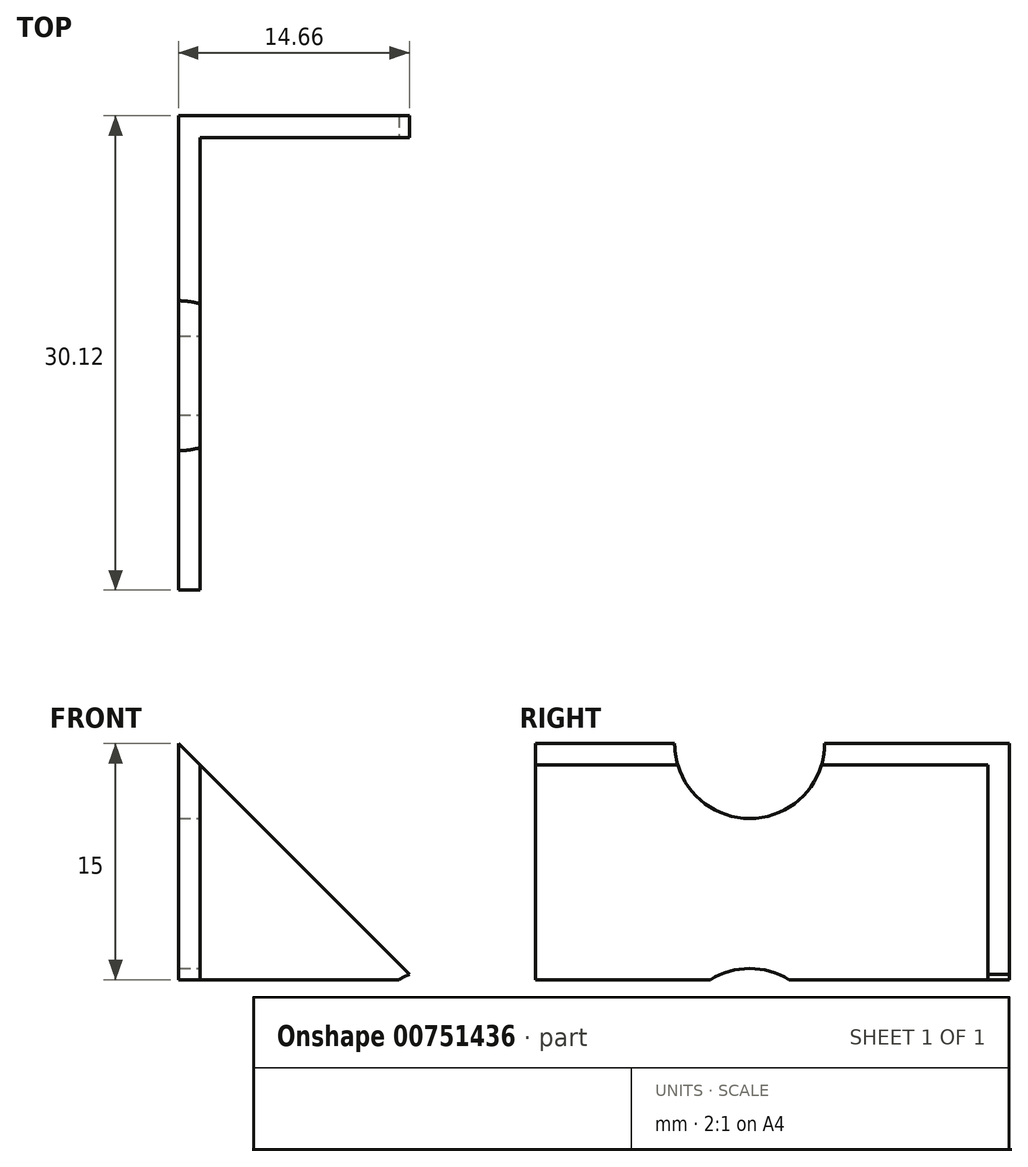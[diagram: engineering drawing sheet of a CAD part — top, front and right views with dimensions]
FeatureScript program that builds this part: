
annotation { "Feature Type Name" : "Feature", "Feature Type Description" : "" }
export const myFeature = defineFeature(function(context is Context, id is Id, definition is map)
    precondition{}
    {
        {
            assignVariable(context, id + "F0", {"name" : "height", "anyValue" : 15});
        }
        {
            var Q0;
            Q0=qCreatedBy(makeId("Top.planeOp"),FACE);
            var sketch = newSketch(context, id + "F1", { "sketchPlane" : qUnion([Q0])});
            skLineSegment(sketch, "E0", {"start": v(-1.37, -28.75) * mm, "end": v(-1.37, 1.37) * mm});
            skLineSegment(sketch, "E1", {"start": v(-1.37, 1.37) * mm, "end": v(28.75, 1.37) * mm});
            skLineSegment(sketch, "E2", {"start": v(28.75, 1.37) * mm, "end": v(28.75, 0) * mm});
            skLineSegment(sketch, "E3", {"start": v(28.75, 0) * mm, "end": v(0, 0) * mm});
            skLineSegment(sketch, "E4", {"start": v(0, 0) * mm, "end": v(0, -28.75) * mm});
            skLineSegment(sketch, "E5", {"start": v(0, -28.75) * mm, "end": v(-1.37, -28.75) * mm});
            skSolve(sketch);
        }
        {
            var Q0;
            Q0=makeQuery(id+"F1.imprint","IMPRINT",FACE,{"disambiguationData":[TD([[makeQuery(id+"F1.imprint","IMPRINT",EDGE,{"derivedFrom":sQuery(id+"F1.wireOp",EDGE,"E0")}),-1.0]])]});
            extrude(context, id + "F2", {"entities" : qUnion([Q0]), "depth" : (getVariable(context, 'height')) * mm, "offsetDistance" : 25.4 * mm});
        }
        {
            var Q0;
            Q0=makeQuery(id+"F2.opExtrude","SWEPT_FACE",FACE,{"disambiguationData":[OSD([sQuery(id+"F1.wireOp",EDGE,"E3")])]});
            var sketch = newSketch(context, id + "F3", { "sketchPlane" : qUnion([Q0])});
            skPoint(sketch, "E6", {"position": v(15.14, 19.05) * mm});
            skLineSegment(sketch, "E7", {"start": v(15.14, 0) * mm, "end": v(15.14, 381) * mm, "construction": true});
            skCircle(sketch, "E8", {"center": v(15.14, 19.05) * mm, "radius": 4.76 * mm});
            skCircle(sketch, "E9", {"center": v(15.14, 0) * mm, "radius": 4.76 * mm});
            skPoint(sketch, "E10", {"position": v(15.14, 38.1) * mm});
            skPoint(sketch, "E11", {"position": v(15.14, 57.15) * mm});
            skArc(sketch, "E12", {"start": v(19.9, 39.69) * mm, "mid": v(15.14, 44.45) * mm, "end": v(10.38, 39.69) * mm});
            skArc(sketch, "E13", {"start": v(10.38, 36.51) * mm, "mid": v(15.14, 31.75) * mm, "end": v(19.9, 36.51) * mm});
            skLineSegment(sketch, "E14", {"start": v(19.9, 39.69) * mm, "end": v(19.9, 36.51) * mm});
            skLineSegment(sketch, "E15", {"start": v(10.38, 39.69) * mm, "end": v(10.38, 36.51) * mm});
            skArc(sketch, "E16", {"start": v(19.9, 58.74) * mm, "mid": v(15.14, 63.5) * mm, "end": v(10.38, 58.74) * mm});
            skArc(sketch, "E17", {"start": v(10.38, 55.56) * mm, "mid": v(15.14, 50.8) * mm, "end": v(19.9, 55.56) * mm});
            skLineSegment(sketch, "E18", {"start": v(19.9, 58.74) * mm, "end": v(19.9, 55.56) * mm});
            skLineSegment(sketch, "E19", {"start": v(10.38, 58.74) * mm, "end": v(10.38, 55.56) * mm});
            skPoint(sketch, "E20.0.1.0", {"position": v(15.14, 133.35) * mm});
            skArc(sketch, "E20.0.1.1", {"start": v(19.9, 134.94) * mm, "mid": v(15.14, 139.7) * mm, "end": v(10.38, 134.94) * mm});
            skPoint(sketch, "E20.0.1.2", {"position": v(15.14, 114.3) * mm});
            skPoint(sketch, "E20.0.1.3", {"position": v(15.14, 95.25) * mm});
            skArc(sketch, "E20.0.1.4", {"start": v(10.38, 131.76) * mm, "mid": v(15.14, 127) * mm, "end": v(19.9, 131.76) * mm});
            skCircle(sketch, "E20.0.1.5", {"center": v(15.14, 95.25) * mm, "radius": 4.76 * mm});
            skCircle(sketch, "E20.0.1.6", {"center": v(15.14, 76.2) * mm, "radius": 4.76 * mm});
            skArc(sketch, "E20.0.1.7", {"start": v(19.9, 115.89) * mm, "mid": v(15.14, 120.65) * mm, "end": v(10.38, 115.89) * mm});
            skArc(sketch, "E20.0.1.8", {"start": v(10.38, 112.71) * mm, "mid": v(15.14, 107.95) * mm, "end": v(19.9, 112.71) * mm});
            skPoint(sketch, "E20.0.1.9", {"position": v(15.14, 133.35) * mm});
            skPoint(sketch, "E20.0.1.10", {"position": v(15.14, 114.3) * mm});
            skLineSegment(sketch, "E20.0.1.11", {"start": v(10.38, 134.94) * mm, "end": v(10.38, 131.76) * mm});
            skLineSegment(sketch, "E20.0.1.12", {"start": v(19.9, 134.94) * mm, "end": v(19.9, 131.76) * mm});
            skLineSegment(sketch, "E20.0.1.13", {"start": v(19.9, 115.89) * mm, "end": v(19.9, 112.71) * mm});
            skLineSegment(sketch, "E20.0.1.14", {"start": v(10.38, 115.89) * mm, "end": v(10.38, 112.71) * mm});
            skPoint(sketch, "E20.0.2.0", {"position": v(15.14, 209.55) * mm});
            skArc(sketch, "E20.0.2.1", {"start": v(19.9, 211.14) * mm, "mid": v(15.14, 215.9) * mm, "end": v(10.38, 211.14) * mm});
            skPoint(sketch, "E20.0.2.2", {"position": v(15.14, 190.5) * mm});
            skPoint(sketch, "E20.0.2.3", {"position": v(15.14, 171.45) * mm});
            skArc(sketch, "E20.0.2.4", {"start": v(10.38, 207.96) * mm, "mid": v(15.14, 203.2) * mm, "end": v(19.9, 207.96) * mm});
            skCircle(sketch, "E20.0.2.5", {"center": v(15.14, 171.45) * mm, "radius": 4.76 * mm});
            skCircle(sketch, "E20.0.2.6", {"center": v(15.14, 152.4) * mm, "radius": 4.76 * mm});
            skArc(sketch, "E20.0.2.7", {"start": v(19.9, 192.09) * mm, "mid": v(15.14, 196.85) * mm, "end": v(10.38, 192.09) * mm});
            skArc(sketch, "E20.0.2.8", {"start": v(10.38, 188.91) * mm, "mid": v(15.14, 184.15) * mm, "end": v(19.9, 188.91) * mm});
            skPoint(sketch, "E20.0.2.9", {"position": v(15.14, 209.55) * mm});
            skPoint(sketch, "E20.0.2.10", {"position": v(15.14, 190.5) * mm});
            skLineSegment(sketch, "E20.0.2.11", {"start": v(10.38, 211.14) * mm, "end": v(10.38, 207.96) * mm});
            skLineSegment(sketch, "E20.0.2.12", {"start": v(19.9, 211.14) * mm, "end": v(19.9, 207.96) * mm});
            skLineSegment(sketch, "E20.0.2.13", {"start": v(19.9, 192.09) * mm, "end": v(19.9, 188.91) * mm});
            skLineSegment(sketch, "E20.0.2.14", {"start": v(10.38, 192.09) * mm, "end": v(10.38, 188.91) * mm});
            skPoint(sketch, "E20.0.3.0", {"position": v(15.14, 285.75) * mm});
            skArc(sketch, "E20.0.3.1", {"start": v(19.9, 287.34) * mm, "mid": v(15.14, 292.1) * mm, "end": v(10.38, 287.34) * mm});
            skPoint(sketch, "E20.0.3.2", {"position": v(15.14, 266.7) * mm});
            skPoint(sketch, "E20.0.3.3", {"position": v(15.14, 247.65) * mm});
            skArc(sketch, "E20.0.3.4", {"start": v(10.38, 284.16) * mm, "mid": v(15.14, 279.4) * mm, "end": v(19.9, 284.16) * mm});
            skCircle(sketch, "E20.0.3.5", {"center": v(15.14, 247.65) * mm, "radius": 4.76 * mm});
            skCircle(sketch, "E20.0.3.6", {"center": v(15.14, 228.6) * mm, "radius": 4.76 * mm});
            skArc(sketch, "E20.0.3.7", {"start": v(19.9, 268.29) * mm, "mid": v(15.14, 273.05) * mm, "end": v(10.38, 268.29) * mm});
            skArc(sketch, "E20.0.3.8", {"start": v(10.38, 265.11) * mm, "mid": v(15.14, 260.35) * mm, "end": v(19.9, 265.11) * mm});
            skPoint(sketch, "E20.0.3.9", {"position": v(15.14, 285.75) * mm});
            skPoint(sketch, "E20.0.3.10", {"position": v(15.14, 266.7) * mm});
            skLineSegment(sketch, "E20.0.3.11", {"start": v(10.38, 287.34) * mm, "end": v(10.38, 284.16) * mm});
            skLineSegment(sketch, "E20.0.3.12", {"start": v(19.9, 287.34) * mm, "end": v(19.9, 284.16) * mm});
            skLineSegment(sketch, "E20.0.3.13", {"start": v(19.9, 268.29) * mm, "end": v(19.9, 265.11) * mm});
            skLineSegment(sketch, "E20.0.3.14", {"start": v(10.38, 268.29) * mm, "end": v(10.38, 265.11) * mm});
            skPoint(sketch, "E20.0.4.0", {"position": v(15.14, 361.95) * mm});
            skArc(sketch, "E20.0.4.1", {"start": v(19.9, 363.54) * mm, "mid": v(15.14, 368.3) * mm, "end": v(10.38, 363.54) * mm});
            skPoint(sketch, "E20.0.4.2", {"position": v(15.14, 342.9) * mm});
            skPoint(sketch, "E20.0.4.3", {"position": v(15.14, 323.85) * mm});
            skArc(sketch, "E20.0.4.4", {"start": v(10.38, 360.36) * mm, "mid": v(15.14, 355.6) * mm, "end": v(19.9, 360.36) * mm});
            skCircle(sketch, "E20.0.4.5", {"center": v(15.14, 323.85) * mm, "radius": 4.76 * mm});
            skCircle(sketch, "E20.0.4.6", {"center": v(15.14, 304.8) * mm, "radius": 4.76 * mm});
            skArc(sketch, "E20.0.4.7", {"start": v(19.9, 344.49) * mm, "mid": v(15.14, 349.25) * mm, "end": v(10.38, 344.49) * mm});
            skArc(sketch, "E20.0.4.8", {"start": v(10.38, 341.31) * mm, "mid": v(15.14, 336.55) * mm, "end": v(19.9, 341.31) * mm});
            skPoint(sketch, "E20.0.4.9", {"position": v(15.14, 361.95) * mm});
            skPoint(sketch, "E20.0.4.10", {"position": v(15.14, 342.9) * mm});
            skLineSegment(sketch, "E20.0.4.11", {"start": v(10.38, 363.54) * mm, "end": v(10.38, 360.36) * mm});
            skLineSegment(sketch, "E20.0.4.12", {"start": v(19.9, 363.54) * mm, "end": v(19.9, 360.36) * mm});
            skLineSegment(sketch, "E20.0.4.13", {"start": v(19.9, 344.49) * mm, "end": v(19.9, 341.31) * mm});
            skLineSegment(sketch, "E20.0.4.14", {"start": v(10.38, 344.49) * mm, "end": v(10.38, 341.31) * mm});
            skPoint(sketch, "E20.0.5.0", {"position": v(15.14, 438.15) * mm});
            skArc(sketch, "E20.0.5.1", {"start": v(19.9, 439.74) * mm, "mid": v(15.14, 444.5) * mm, "end": v(10.38, 439.74) * mm});
            skPoint(sketch, "E20.0.5.2", {"position": v(15.14, 419.1) * mm});
            skPoint(sketch, "E20.0.5.3", {"position": v(15.14, 400.05) * mm});
            skArc(sketch, "E20.0.5.4", {"start": v(10.38, 436.56) * mm, "mid": v(15.14, 431.8) * mm, "end": v(19.9, 436.56) * mm});
            skCircle(sketch, "E20.0.5.5", {"center": v(15.14, 400.05) * mm, "radius": 4.76 * mm});
            skCircle(sketch, "E20.0.5.6", {"center": v(15.14, 381) * mm, "radius": 4.76 * mm});
            skArc(sketch, "E20.0.5.7", {"start": v(19.9, 420.69) * mm, "mid": v(15.14, 425.45) * mm, "end": v(10.38, 420.69) * mm});
            skArc(sketch, "E20.0.5.8", {"start": v(10.38, 417.51) * mm, "mid": v(15.14, 412.75) * mm, "end": v(19.9, 417.51) * mm});
            skPoint(sketch, "E20.0.5.9", {"position": v(15.14, 438.15) * mm});
            skPoint(sketch, "E20.0.5.10", {"position": v(15.14, 419.1) * mm});
            skLineSegment(sketch, "E20.0.5.11", {"start": v(10.38, 439.74) * mm, "end": v(10.38, 436.56) * mm});
            skLineSegment(sketch, "E20.0.5.12", {"start": v(19.9, 439.74) * mm, "end": v(19.9, 436.56) * mm});
            skLineSegment(sketch, "E20.0.5.13", {"start": v(19.9, 420.69) * mm, "end": v(19.9, 417.51) * mm});
            skLineSegment(sketch, "E20.0.5.14", {"start": v(10.38, 420.69) * mm, "end": v(10.38, 417.51) * mm});
            skPoint(sketch, "E20.0.6.0", {"position": v(15.14, 514.35) * mm});
            skArc(sketch, "E20.0.6.1", {"start": v(19.9, 515.94) * mm, "mid": v(15.14, 520.7) * mm, "end": v(10.38, 515.94) * mm});
            skPoint(sketch, "E20.0.6.2", {"position": v(15.14, 495.3) * mm});
            skPoint(sketch, "E20.0.6.3", {"position": v(15.14, 476.25) * mm});
            skArc(sketch, "E20.0.6.4", {"start": v(10.38, 512.76) * mm, "mid": v(15.14, 508) * mm, "end": v(19.9, 512.76) * mm});
            skCircle(sketch, "E20.0.6.5", {"center": v(15.14, 476.25) * mm, "radius": 4.76 * mm});
            skCircle(sketch, "E20.0.6.6", {"center": v(15.14, 457.2) * mm, "radius": 4.76 * mm});
            skArc(sketch, "E20.0.6.7", {"start": v(19.9, 496.89) * mm, "mid": v(15.14, 501.65) * mm, "end": v(10.38, 496.89) * mm});
            skArc(sketch, "E20.0.6.8", {"start": v(10.38, 493.71) * mm, "mid": v(15.14, 488.95) * mm, "end": v(19.9, 493.71) * mm});
            skPoint(sketch, "E20.0.6.9", {"position": v(15.14, 514.35) * mm});
            skPoint(sketch, "E20.0.6.10", {"position": v(15.14, 495.3) * mm});
            skLineSegment(sketch, "E20.0.6.11", {"start": v(10.38, 515.94) * mm, "end": v(10.38, 512.76) * mm});
            skLineSegment(sketch, "E20.0.6.12", {"start": v(19.9, 515.94) * mm, "end": v(19.9, 512.76) * mm});
            skLineSegment(sketch, "E20.0.6.13", {"start": v(19.9, 496.89) * mm, "end": v(19.9, 493.71) * mm});
            skLineSegment(sketch, "E20.0.6.14", {"start": v(10.38, 496.89) * mm, "end": v(10.38, 493.71) * mm});
            skPoint(sketch, "E20.0.7.0", {"position": v(15.14, 590.55) * mm});
            skArc(sketch, "E20.0.7.1", {"start": v(19.9, 592.14) * mm, "mid": v(15.14, 596.9) * mm, "end": v(10.38, 592.14) * mm});
            skPoint(sketch, "E20.0.7.2", {"position": v(15.14, 571.5) * mm});
            skPoint(sketch, "E20.0.7.3", {"position": v(15.14, 552.45) * mm});
            skArc(sketch, "E20.0.7.4", {"start": v(10.38, 588.96) * mm, "mid": v(15.14, 584.2) * mm, "end": v(19.9, 588.96) * mm});
            skCircle(sketch, "E20.0.7.5", {"center": v(15.14, 552.45) * mm, "radius": 4.76 * mm});
            skCircle(sketch, "E20.0.7.6", {"center": v(15.14, 533.4) * mm, "radius": 4.76 * mm});
            skArc(sketch, "E20.0.7.7", {"start": v(19.9, 573.09) * mm, "mid": v(15.14, 577.85) * mm, "end": v(10.38, 573.09) * mm});
            skArc(sketch, "E20.0.7.8", {"start": v(10.38, 569.91) * mm, "mid": v(15.14, 565.15) * mm, "end": v(19.9, 569.91) * mm});
            skPoint(sketch, "E20.0.7.9", {"position": v(15.14, 590.55) * mm});
            skPoint(sketch, "E20.0.7.10", {"position": v(15.14, 571.5) * mm});
            skLineSegment(sketch, "E20.0.7.11", {"start": v(10.38, 592.14) * mm, "end": v(10.38, 588.96) * mm});
            skLineSegment(sketch, "E20.0.7.12", {"start": v(19.9, 592.14) * mm, "end": v(19.9, 588.96) * mm});
            skLineSegment(sketch, "E20.0.7.13", {"start": v(19.9, 573.09) * mm, "end": v(19.9, 569.91) * mm});
            skLineSegment(sketch, "E20.0.7.14", {"start": v(10.38, 573.09) * mm, "end": v(10.38, 569.91) * mm});
            skPoint(sketch, "E20.0.8.0", {"position": v(15.14, 666.75) * mm});
            skArc(sketch, "E20.0.8.1", {"start": v(19.9, 668.34) * mm, "mid": v(15.14, 673.1) * mm, "end": v(10.38, 668.34) * mm});
            skPoint(sketch, "E20.0.8.2", {"position": v(15.14, 647.7) * mm});
            skPoint(sketch, "E20.0.8.3", {"position": v(15.14, 628.65) * mm});
            skArc(sketch, "E20.0.8.4", {"start": v(10.38, 665.16) * mm, "mid": v(15.14, 660.4) * mm, "end": v(19.9, 665.16) * mm});
            skCircle(sketch, "E20.0.8.5", {"center": v(15.14, 628.65) * mm, "radius": 4.76 * mm});
            skCircle(sketch, "E20.0.8.6", {"center": v(15.14, 609.6) * mm, "radius": 4.76 * mm});
            skArc(sketch, "E20.0.8.7", {"start": v(19.9, 649.29) * mm, "mid": v(15.14, 654.05) * mm, "end": v(10.38, 649.29) * mm});
            skArc(sketch, "E20.0.8.8", {"start": v(10.38, 646.11) * mm, "mid": v(15.14, 641.35) * mm, "end": v(19.9, 646.11) * mm});
            skPoint(sketch, "E20.0.8.9", {"position": v(15.14, 666.75) * mm});
            skPoint(sketch, "E20.0.8.10", {"position": v(15.14, 647.7) * mm});
            skLineSegment(sketch, "E20.0.8.11", {"start": v(10.38, 668.34) * mm, "end": v(10.38, 665.16) * mm});
            skLineSegment(sketch, "E20.0.8.12", {"start": v(19.9, 668.34) * mm, "end": v(19.9, 665.16) * mm});
            skLineSegment(sketch, "E20.0.8.13", {"start": v(19.9, 649.29) * mm, "end": v(19.9, 646.11) * mm});
            skLineSegment(sketch, "E20.0.8.14", {"start": v(10.38, 649.29) * mm, "end": v(10.38, 646.11) * mm});
            skPoint(sketch, "E20.0.9.0", {"position": v(15.14, 742.95) * mm});
            skArc(sketch, "E20.0.9.1", {"start": v(19.9, 744.54) * mm, "mid": v(15.14, 749.3) * mm, "end": v(10.38, 744.54) * mm});
            skPoint(sketch, "E20.0.9.2", {"position": v(15.14, 723.9) * mm});
            skPoint(sketch, "E20.0.9.3", {"position": v(15.14, 704.85) * mm});
            skArc(sketch, "E20.0.9.4", {"start": v(10.38, 741.36) * mm, "mid": v(15.14, 736.6) * mm, "end": v(19.9, 741.36) * mm});
            skCircle(sketch, "E20.0.9.5", {"center": v(15.14, 704.85) * mm, "radius": 4.76 * mm});
            skCircle(sketch, "E20.0.9.6", {"center": v(15.14, 685.8) * mm, "radius": 4.76 * mm});
            skArc(sketch, "E20.0.9.7", {"start": v(19.9, 725.49) * mm, "mid": v(15.14, 730.25) * mm, "end": v(10.38, 725.49) * mm});
            skArc(sketch, "E20.0.9.8", {"start": v(10.38, 722.31) * mm, "mid": v(15.14, 717.55) * mm, "end": v(19.9, 722.31) * mm});
            skPoint(sketch, "E20.0.9.9", {"position": v(15.14, 742.95) * mm});
            skPoint(sketch, "E20.0.9.10", {"position": v(15.14, 723.9) * mm});
            skLineSegment(sketch, "E20.0.9.11", {"start": v(10.38, 744.54) * mm, "end": v(10.38, 741.36) * mm});
            skLineSegment(sketch, "E20.0.9.12", {"start": v(19.9, 744.54) * mm, "end": v(19.9, 741.36) * mm});
            skLineSegment(sketch, "E20.0.9.13", {"start": v(19.9, 725.49) * mm, "end": v(19.9, 722.31) * mm});
            skLineSegment(sketch, "E20.0.9.14", {"start": v(10.38, 725.49) * mm, "end": v(10.38, 722.31) * mm});
            skPoint(sketch, "E20.0.10.0", {"position": v(15.14, 819.15) * mm});
            skArc(sketch, "E20.0.10.1", {"start": v(19.9, 820.74) * mm, "mid": v(15.14, 825.5) * mm, "end": v(10.38, 820.74) * mm});
            skPoint(sketch, "E20.0.10.2", {"position": v(15.14, 800.1) * mm});
            skPoint(sketch, "E20.0.10.3", {"position": v(15.14, 781.05) * mm});
            skArc(sketch, "E20.0.10.4", {"start": v(10.38, 817.56) * mm, "mid": v(15.14, 812.8) * mm, "end": v(19.9, 817.56) * mm});
            skCircle(sketch, "E20.0.10.5", {"center": v(15.14, 781.05) * mm, "radius": 4.76 * mm});
            skCircle(sketch, "E20.0.10.6", {"center": v(15.14, 762) * mm, "radius": 4.76 * mm});
            skArc(sketch, "E20.0.10.7", {"start": v(19.9, 801.69) * mm, "mid": v(15.14, 806.45) * mm, "end": v(10.38, 801.69) * mm});
            skArc(sketch, "E20.0.10.8", {"start": v(10.38, 798.51) * mm, "mid": v(15.14, 793.75) * mm, "end": v(19.9, 798.51) * mm});
            skPoint(sketch, "E20.0.10.9", {"position": v(15.14, 819.15) * mm});
            skPoint(sketch, "E20.0.10.10", {"position": v(15.14, 800.1) * mm});
            skLineSegment(sketch, "E20.0.10.11", {"start": v(10.38, 820.74) * mm, "end": v(10.38, 817.56) * mm});
            skLineSegment(sketch, "E20.0.10.12", {"start": v(19.9, 820.74) * mm, "end": v(19.9, 817.56) * mm});
            skLineSegment(sketch, "E20.0.10.13", {"start": v(19.9, 801.69) * mm, "end": v(19.9, 798.51) * mm});
            skLineSegment(sketch, "E20.0.10.14", {"start": v(10.38, 801.69) * mm, "end": v(10.38, 798.51) * mm});
            skPoint(sketch, "E20.0.11.0", {"position": v(15.14, 895.35) * mm});
            skArc(sketch, "E20.0.11.1", {"start": v(19.9, 896.94) * mm, "mid": v(15.14, 901.7) * mm, "end": v(10.38, 896.94) * mm});
            skPoint(sketch, "E20.0.11.2", {"position": v(15.14, 876.3) * mm});
            skPoint(sketch, "E20.0.11.3", {"position": v(15.14, 857.25) * mm});
            skArc(sketch, "E20.0.11.4", {"start": v(10.38, 893.76) * mm, "mid": v(15.14, 889) * mm, "end": v(19.9, 893.76) * mm});
            skCircle(sketch, "E20.0.11.5", {"center": v(15.14, 857.25) * mm, "radius": 4.76 * mm});
            skCircle(sketch, "E20.0.11.6", {"center": v(15.14, 838.2) * mm, "radius": 4.76 * mm});
            skArc(sketch, "E20.0.11.7", {"start": v(19.9, 877.89) * mm, "mid": v(15.14, 882.65) * mm, "end": v(10.38, 877.89) * mm});
            skArc(sketch, "E20.0.11.8", {"start": v(10.38, 874.71) * mm, "mid": v(15.14, 869.95) * mm, "end": v(19.9, 874.71) * mm});
            skPoint(sketch, "E20.0.11.9", {"position": v(15.14, 895.35) * mm});
            skPoint(sketch, "E20.0.11.10", {"position": v(15.14, 876.3) * mm});
            skLineSegment(sketch, "E20.0.11.11", {"start": v(10.38, 896.94) * mm, "end": v(10.38, 893.76) * mm});
            skLineSegment(sketch, "E20.0.11.12", {"start": v(19.9, 896.94) * mm, "end": v(19.9, 893.76) * mm});
            skLineSegment(sketch, "E20.0.11.13", {"start": v(19.9, 877.89) * mm, "end": v(19.9, 874.71) * mm});
            skLineSegment(sketch, "E20.0.11.14", {"start": v(10.38, 877.89) * mm, "end": v(10.38, 874.71) * mm});
            skPoint(sketch, "E20.0.12.0", {"position": v(15.14, 971.55) * mm});
            skArc(sketch, "E20.0.12.1", {"start": v(19.9, 973.14) * mm, "mid": v(15.14, 977.9) * mm, "end": v(10.38, 973.14) * mm});
            skPoint(sketch, "E20.0.12.2", {"position": v(15.14, 952.5) * mm});
            skPoint(sketch, "E20.0.12.3", {"position": v(15.14, 933.45) * mm});
            skArc(sketch, "E20.0.12.4", {"start": v(10.38, 969.96) * mm, "mid": v(15.14, 965.2) * mm, "end": v(19.9, 969.96) * mm});
            skCircle(sketch, "E20.0.12.5", {"center": v(15.14, 933.45) * mm, "radius": 4.76 * mm});
            skCircle(sketch, "E20.0.12.6", {"center": v(15.14, 914.4) * mm, "radius": 4.76 * mm});
            skArc(sketch, "E20.0.12.7", {"start": v(19.9, 954.09) * mm, "mid": v(15.14, 958.85) * mm, "end": v(10.38, 954.09) * mm});
            skArc(sketch, "E20.0.12.8", {"start": v(10.38, 950.91) * mm, "mid": v(15.14, 946.15) * mm, "end": v(19.9, 950.91) * mm});
            skPoint(sketch, "E20.0.12.9", {"position": v(15.14, 971.55) * mm});
            skPoint(sketch, "E20.0.12.10", {"position": v(15.14, 952.5) * mm});
            skLineSegment(sketch, "E20.0.12.11", {"start": v(10.38, 973.14) * mm, "end": v(10.38, 969.96) * mm});
            skLineSegment(sketch, "E20.0.12.12", {"start": v(19.9, 973.14) * mm, "end": v(19.9, 969.96) * mm});
            skLineSegment(sketch, "E20.0.12.13", {"start": v(19.9, 954.09) * mm, "end": v(19.9, 950.91) * mm});
            skLineSegment(sketch, "E20.0.12.14", {"start": v(10.38, 954.09) * mm, "end": v(10.38, 950.91) * mm});
            skPoint(sketch, "E20.0.13.0", {"position": v(15.14, 1047.75) * mm});
            skArc(sketch, "E20.0.13.1", {"start": v(19.9, 1049.34) * mm, "mid": v(15.14, 1054.1) * mm, "end": v(10.38, 1049.34) * mm});
            skPoint(sketch, "E20.0.13.2", {"position": v(15.14, 1028.7) * mm});
            skPoint(sketch, "E20.0.13.3", {"position": v(15.14, 1009.65) * mm});
            skArc(sketch, "E20.0.13.4", {"start": v(10.38, 1046.16) * mm, "mid": v(15.14, 1041.4) * mm, "end": v(19.9, 1046.16) * mm});
            skCircle(sketch, "E20.0.13.5", {"center": v(15.14, 1009.65) * mm, "radius": 4.76 * mm});
            skCircle(sketch, "E20.0.13.6", {"center": v(15.14, 990.6) * mm, "radius": 4.76 * mm});
            skArc(sketch, "E20.0.13.7", {"start": v(19.9, 1030.29) * mm, "mid": v(15.14, 1035.05) * mm, "end": v(10.38, 1030.29) * mm});
            skArc(sketch, "E20.0.13.8", {"start": v(10.38, 1027.11) * mm, "mid": v(15.14, 1022.35) * mm, "end": v(19.9, 1027.11) * mm});
            skPoint(sketch, "E20.0.13.9", {"position": v(15.14, 1047.75) * mm});
            skPoint(sketch, "E20.0.13.10", {"position": v(15.14, 1028.7) * mm});
            skLineSegment(sketch, "E20.0.13.11", {"start": v(10.38, 1049.34) * mm, "end": v(10.38, 1046.16) * mm});
            skLineSegment(sketch, "E20.0.13.12", {"start": v(19.9, 1049.34) * mm, "end": v(19.9, 1046.16) * mm});
            skLineSegment(sketch, "E20.0.13.13", {"start": v(19.9, 1030.29) * mm, "end": v(19.9, 1027.11) * mm});
            skLineSegment(sketch, "E20.0.13.14", {"start": v(10.38, 1030.29) * mm, "end": v(10.38, 1027.11) * mm});
            skPoint(sketch, "E20.0.14.0", {"position": v(15.14, 1123.95) * mm});
            skArc(sketch, "E20.0.14.1", {"start": v(19.9, 1125.54) * mm, "mid": v(15.14, 1130.3) * mm, "end": v(10.38, 1125.54) * mm});
            skPoint(sketch, "E20.0.14.2", {"position": v(15.14, 1104.9) * mm});
            skPoint(sketch, "E20.0.14.3", {"position": v(15.14, 1085.85) * mm});
            skArc(sketch, "E20.0.14.4", {"start": v(10.38, 1122.36) * mm, "mid": v(15.14, 1117.6) * mm, "end": v(19.9, 1122.36) * mm});
            skCircle(sketch, "E20.0.14.5", {"center": v(15.14, 1085.85) * mm, "radius": 4.76 * mm});
            skCircle(sketch, "E20.0.14.6", {"center": v(15.14, 1066.8) * mm, "radius": 4.76 * mm});
            skArc(sketch, "E20.0.14.7", {"start": v(19.9, 1106.49) * mm, "mid": v(15.14, 1111.25) * mm, "end": v(10.38, 1106.49) * mm});
            skArc(sketch, "E20.0.14.8", {"start": v(10.38, 1103.31) * mm, "mid": v(15.14, 1098.55) * mm, "end": v(19.9, 1103.31) * mm});
            skPoint(sketch, "E20.0.14.9", {"position": v(15.14, 1123.95) * mm});
            skPoint(sketch, "E20.0.14.10", {"position": v(15.14, 1104.9) * mm});
            skLineSegment(sketch, "E20.0.14.11", {"start": v(10.38, 1125.54) * mm, "end": v(10.38, 1122.36) * mm});
            skLineSegment(sketch, "E20.0.14.12", {"start": v(19.9, 1125.54) * mm, "end": v(19.9, 1122.36) * mm});
            skLineSegment(sketch, "E20.0.14.13", {"start": v(19.9, 1106.49) * mm, "end": v(19.9, 1103.31) * mm});
            skLineSegment(sketch, "E20.0.14.14", {"start": v(10.38, 1106.49) * mm, "end": v(10.38, 1103.31) * mm});
            skPoint(sketch, "E20.0.15.0", {"position": v(15.14, 1200.15) * mm});
            skArc(sketch, "E20.0.15.1", {"start": v(19.9, 1201.74) * mm, "mid": v(15.14, 1206.5) * mm, "end": v(10.38, 1201.74) * mm});
            skPoint(sketch, "E20.0.15.2", {"position": v(15.14, 1181.1) * mm});
            skPoint(sketch, "E20.0.15.3", {"position": v(15.14, 1162.05) * mm});
            skArc(sketch, "E20.0.15.4", {"start": v(10.38, 1198.56) * mm, "mid": v(15.14, 1193.8) * mm, "end": v(19.9, 1198.56) * mm});
            skCircle(sketch, "E20.0.15.5", {"center": v(15.14, 1162.05) * mm, "radius": 4.76 * mm});
            skCircle(sketch, "E20.0.15.6", {"center": v(15.14, 1143) * mm, "radius": 4.76 * mm});
            skArc(sketch, "E20.0.15.7", {"start": v(19.9, 1182.69) * mm, "mid": v(15.14, 1187.45) * mm, "end": v(10.38, 1182.69) * mm});
            skArc(sketch, "E20.0.15.8", {"start": v(10.38, 1179.51) * mm, "mid": v(15.14, 1174.75) * mm, "end": v(19.9, 1179.51) * mm});
            skPoint(sketch, "E20.0.15.9", {"position": v(15.14, 1200.15) * mm});
            skPoint(sketch, "E20.0.15.10", {"position": v(15.14, 1181.1) * mm});
            skLineSegment(sketch, "E20.0.15.11", {"start": v(10.38, 1201.74) * mm, "end": v(10.38, 1198.56) * mm});
            skLineSegment(sketch, "E20.0.15.12", {"start": v(19.9, 1201.74) * mm, "end": v(19.9, 1198.56) * mm});
            skLineSegment(sketch, "E20.0.15.13", {"start": v(19.9, 1182.69) * mm, "end": v(19.9, 1179.51) * mm});
            skLineSegment(sketch, "E20.0.15.14", {"start": v(10.38, 1182.69) * mm, "end": v(10.38, 1179.51) * mm});
            skPoint(sketch, "E20.0.16.0", {"position": v(15.14, 1276.35) * mm});
            skArc(sketch, "E20.0.16.1", {"start": v(19.9, 1277.94) * mm, "mid": v(15.14, 1282.7) * mm, "end": v(10.38, 1277.94) * mm});
            skPoint(sketch, "E20.0.16.2", {"position": v(15.14, 1257.3) * mm});
            skPoint(sketch, "E20.0.16.3", {"position": v(15.14, 1238.25) * mm});
            skArc(sketch, "E20.0.16.4", {"start": v(10.38, 1274.76) * mm, "mid": v(15.14, 1270) * mm, "end": v(19.9, 1274.76) * mm});
            skCircle(sketch, "E20.0.16.5", {"center": v(15.14, 1238.25) * mm, "radius": 4.76 * mm});
            skCircle(sketch, "E20.0.16.6", {"center": v(15.14, 1219.2) * mm, "radius": 4.76 * mm});
            skArc(sketch, "E20.0.16.7", {"start": v(19.9, 1258.89) * mm, "mid": v(15.14, 1263.65) * mm, "end": v(10.38, 1258.89) * mm});
            skArc(sketch, "E20.0.16.8", {"start": v(10.38, 1255.71) * mm, "mid": v(15.14, 1250.95) * mm, "end": v(19.9, 1255.71) * mm});
            skPoint(sketch, "E20.0.16.9", {"position": v(15.14, 1276.35) * mm});
            skPoint(sketch, "E20.0.16.10", {"position": v(15.14, 1257.3) * mm});
            skLineSegment(sketch, "E20.0.16.11", {"start": v(10.38, 1277.94) * mm, "end": v(10.38, 1274.76) * mm});
            skLineSegment(sketch, "E20.0.16.12", {"start": v(19.9, 1277.94) * mm, "end": v(19.9, 1274.76) * mm});
            skLineSegment(sketch, "E20.0.16.13", {"start": v(19.9, 1258.89) * mm, "end": v(19.9, 1255.71) * mm});
            skLineSegment(sketch, "E20.0.16.14", {"start": v(10.38, 1258.89) * mm, "end": v(10.38, 1255.71) * mm});
            skPoint(sketch, "E20.0.17.0", {"position": v(15.14, 1352.55) * mm});
            skArc(sketch, "E20.0.17.1", {"start": v(19.9, 1354.14) * mm, "mid": v(15.14, 1358.9) * mm, "end": v(10.38, 1354.14) * mm});
            skPoint(sketch, "E20.0.17.2", {"position": v(15.14, 1333.5) * mm});
            skPoint(sketch, "E20.0.17.3", {"position": v(15.14, 1314.45) * mm});
            skArc(sketch, "E20.0.17.4", {"start": v(10.38, 1350.96) * mm, "mid": v(15.14, 1346.2) * mm, "end": v(19.9, 1350.96) * mm});
            skCircle(sketch, "E20.0.17.5", {"center": v(15.14, 1314.45) * mm, "radius": 4.76 * mm});
            skCircle(sketch, "E20.0.17.6", {"center": v(15.14, 1295.4) * mm, "radius": 4.76 * mm});
            skArc(sketch, "E20.0.17.7", {"start": v(19.9, 1335.09) * mm, "mid": v(15.14, 1339.85) * mm, "end": v(10.38, 1335.09) * mm});
            skArc(sketch, "E20.0.17.8", {"start": v(10.38, 1331.91) * mm, "mid": v(15.14, 1327.15) * mm, "end": v(19.9, 1331.91) * mm});
            skPoint(sketch, "E20.0.17.9", {"position": v(15.14, 1352.55) * mm});
            skPoint(sketch, "E20.0.17.10", {"position": v(15.14, 1333.5) * mm});
            skLineSegment(sketch, "E20.0.17.11", {"start": v(10.38, 1354.14) * mm, "end": v(10.38, 1350.96) * mm});
            skLineSegment(sketch, "E20.0.17.12", {"start": v(19.9, 1354.14) * mm, "end": v(19.9, 1350.96) * mm});
            skLineSegment(sketch, "E20.0.17.13", {"start": v(19.9, 1335.09) * mm, "end": v(19.9, 1331.91) * mm});
            skLineSegment(sketch, "E20.0.17.14", {"start": v(10.38, 1335.09) * mm, "end": v(10.38, 1331.91) * mm});
            skPoint(sketch, "E20.0.18.0", {"position": v(15.14, 1428.75) * mm});
            skArc(sketch, "E20.0.18.1", {"start": v(19.9, 1430.34) * mm, "mid": v(15.14, 1435.1) * mm, "end": v(10.38, 1430.34) * mm});
            skPoint(sketch, "E20.0.18.2", {"position": v(15.14, 1409.7) * mm});
            skPoint(sketch, "E20.0.18.3", {"position": v(15.14, 1390.65) * mm});
            skArc(sketch, "E20.0.18.4", {"start": v(10.38, 1427.16) * mm, "mid": v(15.14, 1422.4) * mm, "end": v(19.9, 1427.16) * mm});
            skCircle(sketch, "E20.0.18.5", {"center": v(15.14, 1390.65) * mm, "radius": 4.76 * mm});
            skCircle(sketch, "E20.0.18.6", {"center": v(15.14, 1371.6) * mm, "radius": 4.76 * mm});
            skArc(sketch, "E20.0.18.7", {"start": v(19.9, 1411.29) * mm, "mid": v(15.14, 1416.05) * mm, "end": v(10.38, 1411.29) * mm});
            skArc(sketch, "E20.0.18.8", {"start": v(10.38, 1408.11) * mm, "mid": v(15.14, 1403.35) * mm, "end": v(19.9, 1408.11) * mm});
            skPoint(sketch, "E20.0.18.9", {"position": v(15.14, 1428.75) * mm});
            skPoint(sketch, "E20.0.18.10", {"position": v(15.14, 1409.7) * mm});
            skLineSegment(sketch, "E20.0.18.11", {"start": v(10.38, 1430.34) * mm, "end": v(10.38, 1427.16) * mm});
            skLineSegment(sketch, "E20.0.18.12", {"start": v(19.9, 1430.34) * mm, "end": v(19.9, 1427.16) * mm});
            skLineSegment(sketch, "E20.0.18.13", {"start": v(19.9, 1411.29) * mm, "end": v(19.9, 1408.11) * mm});
            skLineSegment(sketch, "E20.0.18.14", {"start": v(10.38, 1411.29) * mm, "end": v(10.38, 1408.11) * mm});
            skPoint(sketch, "E20.0.19.0", {"position": v(15.14, 1504.95) * mm});
            skArc(sketch, "E20.0.19.1", {"start": v(19.9, 1506.54) * mm, "mid": v(15.14, 1511.3) * mm, "end": v(10.38, 1506.54) * mm});
            skPoint(sketch, "E20.0.19.2", {"position": v(15.14, 1485.9) * mm});
            skPoint(sketch, "E20.0.19.3", {"position": v(15.14, 1466.85) * mm});
            skArc(sketch, "E20.0.19.4", {"start": v(10.38, 1503.36) * mm, "mid": v(15.14, 1498.6) * mm, "end": v(19.9, 1503.36) * mm});
            skCircle(sketch, "E20.0.19.5", {"center": v(15.14, 1466.85) * mm, "radius": 4.76 * mm});
            skCircle(sketch, "E20.0.19.6", {"center": v(15.14, 1447.8) * mm, "radius": 4.76 * mm});
            skArc(sketch, "E20.0.19.7", {"start": v(19.9, 1487.49) * mm, "mid": v(15.14, 1492.25) * mm, "end": v(10.38, 1487.49) * mm});
            skArc(sketch, "E20.0.19.8", {"start": v(10.38, 1484.31) * mm, "mid": v(15.14, 1479.55) * mm, "end": v(19.9, 1484.31) * mm});
            skPoint(sketch, "E20.0.19.9", {"position": v(15.14, 1504.95) * mm});
            skPoint(sketch, "E20.0.19.10", {"position": v(15.14, 1485.9) * mm});
            skLineSegment(sketch, "E20.0.19.11", {"start": v(10.38, 1506.54) * mm, "end": v(10.38, 1503.36) * mm});
            skLineSegment(sketch, "E20.0.19.12", {"start": v(19.9, 1506.54) * mm, "end": v(19.9, 1503.36) * mm});
            skLineSegment(sketch, "E20.0.19.13", {"start": v(19.9, 1487.49) * mm, "end": v(19.9, 1484.31) * mm});
            skLineSegment(sketch, "E20.0.19.14", {"start": v(10.38, 1487.49) * mm, "end": v(10.38, 1484.31) * mm});
            skPoint(sketch, "E20.0.20.0", {"position": v(15.14, 1581.15) * mm});
            skArc(sketch, "E20.0.20.1", {"start": v(19.9, 1582.74) * mm, "mid": v(15.14, 1587.5) * mm, "end": v(10.38, 1582.74) * mm});
            skPoint(sketch, "E20.0.20.2", {"position": v(15.14, 1562.1) * mm});
            skPoint(sketch, "E20.0.20.3", {"position": v(15.14, 1543.05) * mm});
            skArc(sketch, "E20.0.20.4", {"start": v(10.38, 1579.56) * mm, "mid": v(15.14, 1574.8) * mm, "end": v(19.9, 1579.56) * mm});
            skCircle(sketch, "E20.0.20.5", {"center": v(15.14, 1543.05) * mm, "radius": 4.76 * mm});
            skCircle(sketch, "E20.0.20.6", {"center": v(15.14, 1524) * mm, "radius": 4.76 * mm});
            skArc(sketch, "E20.0.20.7", {"start": v(19.9, 1563.69) * mm, "mid": v(15.14, 1568.45) * mm, "end": v(10.38, 1563.69) * mm});
            skArc(sketch, "E20.0.20.8", {"start": v(10.38, 1560.51) * mm, "mid": v(15.14, 1555.75) * mm, "end": v(19.9, 1560.51) * mm});
            skPoint(sketch, "E20.0.20.9", {"position": v(15.14, 1581.15) * mm});
            skPoint(sketch, "E20.0.20.10", {"position": v(15.14, 1562.1) * mm});
            skLineSegment(sketch, "E20.0.20.11", {"start": v(10.38, 1582.74) * mm, "end": v(10.38, 1579.56) * mm});
            skLineSegment(sketch, "E20.0.20.12", {"start": v(19.9, 1582.74) * mm, "end": v(19.9, 1579.56) * mm});
            skLineSegment(sketch, "E20.0.20.13", {"start": v(19.9, 1563.69) * mm, "end": v(19.9, 1560.51) * mm});
            skLineSegment(sketch, "E20.0.20.14", {"start": v(10.38, 1563.69) * mm, "end": v(10.38, 1560.51) * mm});
            skPoint(sketch, "E20.0.21.0", {"position": v(15.14, 1657.35) * mm});
            skArc(sketch, "E20.0.21.1", {"start": v(19.9, 1658.94) * mm, "mid": v(15.14, 1663.7) * mm, "end": v(10.38, 1658.94) * mm});
            skPoint(sketch, "E20.0.21.2", {"position": v(15.14, 1638.3) * mm});
            skPoint(sketch, "E20.0.21.3", {"position": v(15.14, 1619.25) * mm});
            skArc(sketch, "E20.0.21.4", {"start": v(10.38, 1655.76) * mm, "mid": v(15.14, 1651) * mm, "end": v(19.9, 1655.76) * mm});
            skCircle(sketch, "E20.0.21.5", {"center": v(15.14, 1619.25) * mm, "radius": 4.76 * mm});
            skCircle(sketch, "E20.0.21.6", {"center": v(15.14, 1600.2) * mm, "radius": 4.76 * mm});
            skArc(sketch, "E20.0.21.7", {"start": v(19.9, 1639.89) * mm, "mid": v(15.14, 1644.65) * mm, "end": v(10.38, 1639.89) * mm});
            skArc(sketch, "E20.0.21.8", {"start": v(10.38, 1636.71) * mm, "mid": v(15.14, 1631.95) * mm, "end": v(19.9, 1636.71) * mm});
            skPoint(sketch, "E20.0.21.9", {"position": v(15.14, 1657.35) * mm});
            skPoint(sketch, "E20.0.21.10", {"position": v(15.14, 1638.3) * mm});
            skLineSegment(sketch, "E20.0.21.11", {"start": v(10.38, 1658.94) * mm, "end": v(10.38, 1655.76) * mm});
            skLineSegment(sketch, "E20.0.21.12", {"start": v(19.9, 1658.94) * mm, "end": v(19.9, 1655.76) * mm});
            skLineSegment(sketch, "E20.0.21.13", {"start": v(19.9, 1639.89) * mm, "end": v(19.9, 1636.71) * mm});
            skLineSegment(sketch, "E20.0.21.14", {"start": v(10.38, 1639.89) * mm, "end": v(10.38, 1636.71) * mm});
            skPoint(sketch, "E20.0.22.0", {"position": v(15.14, 1733.55) * mm});
            skArc(sketch, "E20.0.22.1", {"start": v(19.9, 1735.14) * mm, "mid": v(15.14, 1739.9) * mm, "end": v(10.38, 1735.14) * mm});
            skPoint(sketch, "E20.0.22.2", {"position": v(15.14, 1714.5) * mm});
            skPoint(sketch, "E20.0.22.3", {"position": v(15.14, 1695.45) * mm});
            skArc(sketch, "E20.0.22.4", {"start": v(10.38, 1731.96) * mm, "mid": v(15.14, 1727.2) * mm, "end": v(19.9, 1731.96) * mm});
            skCircle(sketch, "E20.0.22.5", {"center": v(15.14, 1695.45) * mm, "radius": 4.76 * mm});
            skCircle(sketch, "E20.0.22.6", {"center": v(15.14, 1676.4) * mm, "radius": 4.76 * mm});
            skArc(sketch, "E20.0.22.7", {"start": v(19.9, 1716.09) * mm, "mid": v(15.14, 1720.85) * mm, "end": v(10.38, 1716.09) * mm});
            skArc(sketch, "E20.0.22.8", {"start": v(10.38, 1712.91) * mm, "mid": v(15.14, 1708.15) * mm, "end": v(19.9, 1712.91) * mm});
            skPoint(sketch, "E20.0.22.9", {"position": v(15.14, 1733.55) * mm});
            skPoint(sketch, "E20.0.22.10", {"position": v(15.14, 1714.5) * mm});
            skLineSegment(sketch, "E20.0.22.11", {"start": v(10.38, 1735.14) * mm, "end": v(10.38, 1731.96) * mm});
            skLineSegment(sketch, "E20.0.22.12", {"start": v(19.9, 1735.14) * mm, "end": v(19.9, 1731.96) * mm});
            skLineSegment(sketch, "E20.0.22.13", {"start": v(19.9, 1716.09) * mm, "end": v(19.9, 1712.91) * mm});
            skLineSegment(sketch, "E20.0.22.14", {"start": v(10.38, 1716.09) * mm, "end": v(10.38, 1712.91) * mm});
            skPoint(sketch, "E20.0.23.0", {"position": v(15.14, 1809.75) * mm});
            skArc(sketch, "E20.0.23.1", {"start": v(19.9, 1811.34) * mm, "mid": v(15.14, 1816.1) * mm, "end": v(10.38, 1811.34) * mm});
            skPoint(sketch, "E20.0.23.2", {"position": v(15.14, 1790.7) * mm});
            skPoint(sketch, "E20.0.23.3", {"position": v(15.14, 1771.65) * mm});
            skArc(sketch, "E20.0.23.4", {"start": v(10.38, 1808.16) * mm, "mid": v(15.14, 1803.4) * mm, "end": v(19.9, 1808.16) * mm});
            skCircle(sketch, "E20.0.23.5", {"center": v(15.14, 1771.65) * mm, "radius": 4.76 * mm});
            skCircle(sketch, "E20.0.23.6", {"center": v(15.14, 1752.6) * mm, "radius": 4.76 * mm});
            skArc(sketch, "E20.0.23.7", {"start": v(19.9, 1792.29) * mm, "mid": v(15.14, 1797.05) * mm, "end": v(10.38, 1792.29) * mm});
            skArc(sketch, "E20.0.23.8", {"start": v(10.38, 1789.11) * mm, "mid": v(15.14, 1784.35) * mm, "end": v(19.9, 1789.11) * mm});
            skPoint(sketch, "E20.0.23.9", {"position": v(15.14, 1809.75) * mm});
            skPoint(sketch, "E20.0.23.10", {"position": v(15.14, 1790.7) * mm});
            skLineSegment(sketch, "E20.0.23.11", {"start": v(10.38, 1811.34) * mm, "end": v(10.38, 1808.16) * mm});
            skLineSegment(sketch, "E20.0.23.12", {"start": v(19.9, 1811.34) * mm, "end": v(19.9, 1808.16) * mm});
            skLineSegment(sketch, "E20.0.23.13", {"start": v(19.9, 1792.29) * mm, "end": v(19.9, 1789.11) * mm});
            skLineSegment(sketch, "E20.0.23.14", {"start": v(10.38, 1792.29) * mm, "end": v(10.38, 1789.11) * mm});
            skLineSegment(sketch, "E20.direction1", {"start": v(15.14, 0) * mm, "end": v(40.54, 0) * mm, "construction": true});
            skLineSegment(sketch, "E20.direction2", {"start": v(15.14, 0) * mm, "end": v(15.14, 76.2) * mm, "construction": true});
            skSolve(sketch);
        }
        {
            var Q0;
            Q0=makeQuery(id+"F2.opExtrude","SWEPT_FACE",FACE,{"disambiguationData":[OSD([sQuery(id+"F1.wireOp",EDGE,"E4")])]});
            var sketch = newSketch(context, id + "F4", { "sketchPlane" : qUnion([Q0])});
            skPoint(sketch, "E21", {"position": v(-15.14, 19.05) * mm});
            skLineSegment(sketch, "E22", {"start": v(-15.14, 0) * mm, "end": v(-15.14, 381) * mm, "construction": true});
            skCircle(sketch, "E23", {"center": v(-15.14, 19.05) * mm, "radius": 4.76 * mm});
            skCircle(sketch, "E24", {"center": v(-15.14, 0) * mm, "radius": 4.76 * mm});
            skPoint(sketch, "E25", {"position": v(-15.14, 38.1) * mm});
            skPoint(sketch, "E26", {"position": v(-15.14, 57.15) * mm});
            skArc(sketch, "E27", {"start": v(-10.38, 39.69) * mm, "mid": v(-15.14, 44.45) * mm, "end": v(-19.9, 39.69) * mm});
            skArc(sketch, "E28", {"start": v(-19.9, 36.51) * mm, "mid": v(-15.14, 31.75) * mm, "end": v(-10.38, 36.51) * mm});
            skLineSegment(sketch, "E29", {"start": v(-10.38, 39.69) * mm, "end": v(-10.38, 36.51) * mm});
            skLineSegment(sketch, "E30", {"start": v(-19.9, 39.69) * mm, "end": v(-19.9, 36.51) * mm});
            skArc(sketch, "E31", {"start": v(-10.38, 58.74) * mm, "mid": v(-15.14, 63.5) * mm, "end": v(-19.9, 58.74) * mm});
            skArc(sketch, "E32", {"start": v(-19.9, 55.56) * mm, "mid": v(-15.14, 50.8) * mm, "end": v(-10.38, 55.56) * mm});
            skLineSegment(sketch, "E33", {"start": v(-10.38, 58.74) * mm, "end": v(-10.38, 55.56) * mm});
            skLineSegment(sketch, "E34", {"start": v(-19.9, 58.74) * mm, "end": v(-19.9, 55.56) * mm});
            skPoint(sketch, "E35.0.1.0", {"position": v(-15.14, 133.35) * mm});
            skArc(sketch, "E35.0.1.1", {"start": v(-10.38, 134.94) * mm, "mid": v(-15.14, 139.7) * mm, "end": v(-19.9, 134.94) * mm});
            skPoint(sketch, "E35.0.1.2", {"position": v(-15.14, 114.3) * mm});
            skPoint(sketch, "E35.0.1.3", {"position": v(-15.14, 95.25) * mm});
            skArc(sketch, "E35.0.1.4", {"start": v(-19.9, 131.76) * mm, "mid": v(-15.14, 127) * mm, "end": v(-10.38, 131.76) * mm});
            skCircle(sketch, "E35.0.1.5", {"center": v(-15.14, 95.25) * mm, "radius": 4.76 * mm});
            skCircle(sketch, "E35.0.1.6", {"center": v(-15.14, 76.2) * mm, "radius": 4.76 * mm});
            skArc(sketch, "E35.0.1.7", {"start": v(-10.38, 115.89) * mm, "mid": v(-15.14, 120.65) * mm, "end": v(-19.9, 115.89) * mm});
            skArc(sketch, "E35.0.1.8", {"start": v(-19.9, 112.71) * mm, "mid": v(-15.14, 107.95) * mm, "end": v(-10.38, 112.71) * mm});
            skPoint(sketch, "E35.0.1.9", {"position": v(-15.14, 133.35) * mm});
            skPoint(sketch, "E35.0.1.10", {"position": v(-15.14, 114.3) * mm});
            skLineSegment(sketch, "E35.0.1.11", {"start": v(-19.9, 134.94) * mm, "end": v(-19.9, 131.76) * mm});
            skLineSegment(sketch, "E35.0.1.12", {"start": v(-10.38, 134.94) * mm, "end": v(-10.38, 131.76) * mm});
            skLineSegment(sketch, "E35.0.1.13", {"start": v(-10.38, 115.89) * mm, "end": v(-10.38, 112.71) * mm});
            skLineSegment(sketch, "E35.0.1.14", {"start": v(-19.9, 115.89) * mm, "end": v(-19.9, 112.71) * mm});
            skPoint(sketch, "E35.0.2.0", {"position": v(-15.14, 209.55) * mm});
            skArc(sketch, "E35.0.2.1", {"start": v(-10.38, 211.14) * mm, "mid": v(-15.14, 215.9) * mm, "end": v(-19.9, 211.14) * mm});
            skPoint(sketch, "E35.0.2.2", {"position": v(-15.14, 190.5) * mm});
            skPoint(sketch, "E35.0.2.3", {"position": v(-15.14, 171.45) * mm});
            skArc(sketch, "E35.0.2.4", {"start": v(-19.9, 207.96) * mm, "mid": v(-15.14, 203.2) * mm, "end": v(-10.38, 207.96) * mm});
            skCircle(sketch, "E35.0.2.5", {"center": v(-15.14, 171.45) * mm, "radius": 4.76 * mm});
            skCircle(sketch, "E35.0.2.6", {"center": v(-15.14, 152.4) * mm, "radius": 4.76 * mm});
            skArc(sketch, "E35.0.2.7", {"start": v(-10.38, 192.09) * mm, "mid": v(-15.14, 196.85) * mm, "end": v(-19.9, 192.09) * mm});
            skArc(sketch, "E35.0.2.8", {"start": v(-19.9, 188.91) * mm, "mid": v(-15.14, 184.15) * mm, "end": v(-10.38, 188.91) * mm});
            skPoint(sketch, "E35.0.2.9", {"position": v(-15.14, 209.55) * mm});
            skPoint(sketch, "E35.0.2.10", {"position": v(-15.14, 190.5) * mm});
            skLineSegment(sketch, "E35.0.2.11", {"start": v(-19.9, 211.14) * mm, "end": v(-19.9, 207.96) * mm});
            skLineSegment(sketch, "E35.0.2.12", {"start": v(-10.38, 211.14) * mm, "end": v(-10.38, 207.96) * mm});
            skLineSegment(sketch, "E35.0.2.13", {"start": v(-10.38, 192.09) * mm, "end": v(-10.38, 188.91) * mm});
            skLineSegment(sketch, "E35.0.2.14", {"start": v(-19.9, 192.09) * mm, "end": v(-19.9, 188.91) * mm});
            skPoint(sketch, "E35.0.3.0", {"position": v(-15.14, 285.75) * mm});
            skArc(sketch, "E35.0.3.1", {"start": v(-10.38, 287.34) * mm, "mid": v(-15.14, 292.1) * mm, "end": v(-19.9, 287.34) * mm});
            skPoint(sketch, "E35.0.3.2", {"position": v(-15.14, 266.7) * mm});
            skPoint(sketch, "E35.0.3.3", {"position": v(-15.14, 247.65) * mm});
            skArc(sketch, "E35.0.3.4", {"start": v(-19.9, 284.16) * mm, "mid": v(-15.14, 279.4) * mm, "end": v(-10.38, 284.16) * mm});
            skCircle(sketch, "E35.0.3.5", {"center": v(-15.14, 247.65) * mm, "radius": 4.76 * mm});
            skCircle(sketch, "E35.0.3.6", {"center": v(-15.14, 228.6) * mm, "radius": 4.76 * mm});
            skArc(sketch, "E35.0.3.7", {"start": v(-10.38, 268.29) * mm, "mid": v(-15.14, 273.05) * mm, "end": v(-19.9, 268.29) * mm});
            skArc(sketch, "E35.0.3.8", {"start": v(-19.9, 265.11) * mm, "mid": v(-15.14, 260.35) * mm, "end": v(-10.38, 265.11) * mm});
            skPoint(sketch, "E35.0.3.9", {"position": v(-15.14, 285.75) * mm});
            skPoint(sketch, "E35.0.3.10", {"position": v(-15.14, 266.7) * mm});
            skLineSegment(sketch, "E35.0.3.11", {"start": v(-19.9, 287.34) * mm, "end": v(-19.9, 284.16) * mm});
            skLineSegment(sketch, "E35.0.3.12", {"start": v(-10.38, 287.34) * mm, "end": v(-10.38, 284.16) * mm});
            skLineSegment(sketch, "E35.0.3.13", {"start": v(-10.38, 268.29) * mm, "end": v(-10.38, 265.11) * mm});
            skLineSegment(sketch, "E35.0.3.14", {"start": v(-19.9, 268.29) * mm, "end": v(-19.9, 265.11) * mm});
            skPoint(sketch, "E35.0.4.0", {"position": v(-15.14, 361.95) * mm});
            skArc(sketch, "E35.0.4.1", {"start": v(-10.38, 363.54) * mm, "mid": v(-15.14, 368.3) * mm, "end": v(-19.9, 363.54) * mm});
            skPoint(sketch, "E35.0.4.2", {"position": v(-15.14, 342.9) * mm});
            skPoint(sketch, "E35.0.4.3", {"position": v(-15.14, 323.85) * mm});
            skArc(sketch, "E35.0.4.4", {"start": v(-19.9, 360.36) * mm, "mid": v(-15.14, 355.6) * mm, "end": v(-10.38, 360.36) * mm});
            skCircle(sketch, "E35.0.4.5", {"center": v(-15.14, 323.85) * mm, "radius": 4.76 * mm});
            skCircle(sketch, "E35.0.4.6", {"center": v(-15.14, 304.8) * mm, "radius": 4.76 * mm});
            skArc(sketch, "E35.0.4.7", {"start": v(-10.38, 344.49) * mm, "mid": v(-15.14, 349.25) * mm, "end": v(-19.9, 344.49) * mm});
            skArc(sketch, "E35.0.4.8", {"start": v(-19.9, 341.31) * mm, "mid": v(-15.14, 336.55) * mm, "end": v(-10.38, 341.31) * mm});
            skPoint(sketch, "E35.0.4.9", {"position": v(-15.14, 361.95) * mm});
            skPoint(sketch, "E35.0.4.10", {"position": v(-15.14, 342.9) * mm});
            skLineSegment(sketch, "E35.0.4.11", {"start": v(-19.9, 363.54) * mm, "end": v(-19.9, 360.36) * mm});
            skLineSegment(sketch, "E35.0.4.12", {"start": v(-10.38, 363.54) * mm, "end": v(-10.38, 360.36) * mm});
            skLineSegment(sketch, "E35.0.4.13", {"start": v(-10.38, 344.49) * mm, "end": v(-10.38, 341.31) * mm});
            skLineSegment(sketch, "E35.0.4.14", {"start": v(-19.9, 344.49) * mm, "end": v(-19.9, 341.31) * mm});
            skPoint(sketch, "E35.0.5.0", {"position": v(-15.14, 438.15) * mm});
            skArc(sketch, "E35.0.5.1", {"start": v(-10.38, 439.74) * mm, "mid": v(-15.14, 444.5) * mm, "end": v(-19.9, 439.74) * mm});
            skPoint(sketch, "E35.0.5.2", {"position": v(-15.14, 419.1) * mm});
            skPoint(sketch, "E35.0.5.3", {"position": v(-15.14, 400.05) * mm});
            skArc(sketch, "E35.0.5.4", {"start": v(-19.9, 436.56) * mm, "mid": v(-15.14, 431.8) * mm, "end": v(-10.38, 436.56) * mm});
            skCircle(sketch, "E35.0.5.5", {"center": v(-15.14, 400.05) * mm, "radius": 4.76 * mm});
            skCircle(sketch, "E35.0.5.6", {"center": v(-15.14, 381) * mm, "radius": 4.76 * mm});
            skArc(sketch, "E35.0.5.7", {"start": v(-10.38, 420.69) * mm, "mid": v(-15.14, 425.45) * mm, "end": v(-19.9, 420.69) * mm});
            skArc(sketch, "E35.0.5.8", {"start": v(-19.9, 417.51) * mm, "mid": v(-15.14, 412.75) * mm, "end": v(-10.38, 417.51) * mm});
            skPoint(sketch, "E35.0.5.9", {"position": v(-15.14, 438.15) * mm});
            skPoint(sketch, "E35.0.5.10", {"position": v(-15.14, 419.1) * mm});
            skLineSegment(sketch, "E35.0.5.11", {"start": v(-19.9, 439.74) * mm, "end": v(-19.9, 436.56) * mm});
            skLineSegment(sketch, "E35.0.5.12", {"start": v(-10.38, 439.74) * mm, "end": v(-10.38, 436.56) * mm});
            skLineSegment(sketch, "E35.0.5.13", {"start": v(-10.38, 420.69) * mm, "end": v(-10.38, 417.51) * mm});
            skLineSegment(sketch, "E35.0.5.14", {"start": v(-19.9, 420.69) * mm, "end": v(-19.9, 417.51) * mm});
            skPoint(sketch, "E35.0.6.0", {"position": v(-15.14, 514.35) * mm});
            skArc(sketch, "E35.0.6.1", {"start": v(-10.38, 515.94) * mm, "mid": v(-15.14, 520.7) * mm, "end": v(-19.9, 515.94) * mm});
            skPoint(sketch, "E35.0.6.2", {"position": v(-15.14, 495.3) * mm});
            skPoint(sketch, "E35.0.6.3", {"position": v(-15.14, 476.25) * mm});
            skArc(sketch, "E35.0.6.4", {"start": v(-19.9, 512.76) * mm, "mid": v(-15.14, 508) * mm, "end": v(-10.38, 512.76) * mm});
            skCircle(sketch, "E35.0.6.5", {"center": v(-15.14, 476.25) * mm, "radius": 4.76 * mm});
            skCircle(sketch, "E35.0.6.6", {"center": v(-15.14, 457.2) * mm, "radius": 4.76 * mm});
            skArc(sketch, "E35.0.6.7", {"start": v(-10.38, 496.89) * mm, "mid": v(-15.14, 501.65) * mm, "end": v(-19.9, 496.89) * mm});
            skArc(sketch, "E35.0.6.8", {"start": v(-19.9, 493.71) * mm, "mid": v(-15.14, 488.95) * mm, "end": v(-10.38, 493.71) * mm});
            skPoint(sketch, "E35.0.6.9", {"position": v(-15.14, 514.35) * mm});
            skPoint(sketch, "E35.0.6.10", {"position": v(-15.14, 495.3) * mm});
            skLineSegment(sketch, "E35.0.6.11", {"start": v(-19.9, 515.94) * mm, "end": v(-19.9, 512.76) * mm});
            skLineSegment(sketch, "E35.0.6.12", {"start": v(-10.38, 515.94) * mm, "end": v(-10.38, 512.76) * mm});
            skLineSegment(sketch, "E35.0.6.13", {"start": v(-10.38, 496.89) * mm, "end": v(-10.38, 493.71) * mm});
            skLineSegment(sketch, "E35.0.6.14", {"start": v(-19.9, 496.89) * mm, "end": v(-19.9, 493.71) * mm});
            skPoint(sketch, "E35.0.7.0", {"position": v(-15.14, 590.55) * mm});
            skArc(sketch, "E35.0.7.1", {"start": v(-10.38, 592.14) * mm, "mid": v(-15.14, 596.9) * mm, "end": v(-19.9, 592.14) * mm});
            skPoint(sketch, "E35.0.7.2", {"position": v(-15.14, 571.5) * mm});
            skPoint(sketch, "E35.0.7.3", {"position": v(-15.14, 552.45) * mm});
            skArc(sketch, "E35.0.7.4", {"start": v(-19.9, 588.96) * mm, "mid": v(-15.14, 584.2) * mm, "end": v(-10.38, 588.96) * mm});
            skCircle(sketch, "E35.0.7.5", {"center": v(-15.14, 552.45) * mm, "radius": 4.76 * mm});
            skCircle(sketch, "E35.0.7.6", {"center": v(-15.14, 533.4) * mm, "radius": 4.76 * mm});
            skArc(sketch, "E35.0.7.7", {"start": v(-10.38, 573.09) * mm, "mid": v(-15.14, 577.85) * mm, "end": v(-19.9, 573.09) * mm});
            skArc(sketch, "E35.0.7.8", {"start": v(-19.9, 569.91) * mm, "mid": v(-15.14, 565.15) * mm, "end": v(-10.38, 569.91) * mm});
            skPoint(sketch, "E35.0.7.9", {"position": v(-15.14, 590.55) * mm});
            skPoint(sketch, "E35.0.7.10", {"position": v(-15.14, 571.5) * mm});
            skLineSegment(sketch, "E35.0.7.11", {"start": v(-19.9, 592.14) * mm, "end": v(-19.9, 588.96) * mm});
            skLineSegment(sketch, "E35.0.7.12", {"start": v(-10.38, 592.14) * mm, "end": v(-10.38, 588.96) * mm});
            skLineSegment(sketch, "E35.0.7.13", {"start": v(-10.38, 573.09) * mm, "end": v(-10.38, 569.91) * mm});
            skLineSegment(sketch, "E35.0.7.14", {"start": v(-19.9, 573.09) * mm, "end": v(-19.9, 569.91) * mm});
            skPoint(sketch, "E35.0.8.0", {"position": v(-15.14, 666.75) * mm});
            skArc(sketch, "E35.0.8.1", {"start": v(-10.38, 668.34) * mm, "mid": v(-15.14, 673.1) * mm, "end": v(-19.9, 668.34) * mm});
            skPoint(sketch, "E35.0.8.2", {"position": v(-15.14, 647.7) * mm});
            skPoint(sketch, "E35.0.8.3", {"position": v(-15.14, 628.65) * mm});
            skArc(sketch, "E35.0.8.4", {"start": v(-19.9, 665.16) * mm, "mid": v(-15.14, 660.4) * mm, "end": v(-10.38, 665.16) * mm});
            skCircle(sketch, "E35.0.8.5", {"center": v(-15.14, 628.65) * mm, "radius": 4.76 * mm});
            skCircle(sketch, "E35.0.8.6", {"center": v(-15.14, 609.6) * mm, "radius": 4.76 * mm});
            skArc(sketch, "E35.0.8.7", {"start": v(-10.38, 649.29) * mm, "mid": v(-15.14, 654.05) * mm, "end": v(-19.9, 649.29) * mm});
            skArc(sketch, "E35.0.8.8", {"start": v(-19.9, 646.11) * mm, "mid": v(-15.14, 641.35) * mm, "end": v(-10.38, 646.11) * mm});
            skPoint(sketch, "E35.0.8.9", {"position": v(-15.14, 666.75) * mm});
            skPoint(sketch, "E35.0.8.10", {"position": v(-15.14, 647.7) * mm});
            skLineSegment(sketch, "E35.0.8.11", {"start": v(-19.9, 668.34) * mm, "end": v(-19.9, 665.16) * mm});
            skLineSegment(sketch, "E35.0.8.12", {"start": v(-10.38, 668.34) * mm, "end": v(-10.38, 665.16) * mm});
            skLineSegment(sketch, "E35.0.8.13", {"start": v(-10.38, 649.29) * mm, "end": v(-10.38, 646.11) * mm});
            skLineSegment(sketch, "E35.0.8.14", {"start": v(-19.9, 649.29) * mm, "end": v(-19.9, 646.11) * mm});
            skPoint(sketch, "E35.0.9.0", {"position": v(-15.14, 742.95) * mm});
            skArc(sketch, "E35.0.9.1", {"start": v(-10.38, 744.54) * mm, "mid": v(-15.14, 749.3) * mm, "end": v(-19.9, 744.54) * mm});
            skPoint(sketch, "E35.0.9.2", {"position": v(-15.14, 723.9) * mm});
            skPoint(sketch, "E35.0.9.3", {"position": v(-15.14, 704.85) * mm});
            skArc(sketch, "E35.0.9.4", {"start": v(-19.9, 741.36) * mm, "mid": v(-15.14, 736.6) * mm, "end": v(-10.38, 741.36) * mm});
            skCircle(sketch, "E35.0.9.5", {"center": v(-15.14, 704.85) * mm, "radius": 4.76 * mm});
            skCircle(sketch, "E35.0.9.6", {"center": v(-15.14, 685.8) * mm, "radius": 4.76 * mm});
            skArc(sketch, "E35.0.9.7", {"start": v(-10.38, 725.49) * mm, "mid": v(-15.14, 730.25) * mm, "end": v(-19.9, 725.49) * mm});
            skArc(sketch, "E35.0.9.8", {"start": v(-19.9, 722.31) * mm, "mid": v(-15.14, 717.55) * mm, "end": v(-10.38, 722.31) * mm});
            skPoint(sketch, "E35.0.9.9", {"position": v(-15.14, 742.95) * mm});
            skPoint(sketch, "E35.0.9.10", {"position": v(-15.14, 723.9) * mm});
            skLineSegment(sketch, "E35.0.9.11", {"start": v(-19.9, 744.54) * mm, "end": v(-19.9, 741.36) * mm});
            skLineSegment(sketch, "E35.0.9.12", {"start": v(-10.38, 744.54) * mm, "end": v(-10.38, 741.36) * mm});
            skLineSegment(sketch, "E35.0.9.13", {"start": v(-10.38, 725.49) * mm, "end": v(-10.38, 722.31) * mm});
            skLineSegment(sketch, "E35.0.9.14", {"start": v(-19.9, 725.49) * mm, "end": v(-19.9, 722.31) * mm});
            skPoint(sketch, "E35.0.10.0", {"position": v(-15.14, 819.15) * mm});
            skArc(sketch, "E35.0.10.1", {"start": v(-10.38, 820.74) * mm, "mid": v(-15.14, 825.5) * mm, "end": v(-19.9, 820.74) * mm});
            skPoint(sketch, "E35.0.10.2", {"position": v(-15.14, 800.1) * mm});
            skPoint(sketch, "E35.0.10.3", {"position": v(-15.14, 781.05) * mm});
            skArc(sketch, "E35.0.10.4", {"start": v(-19.9, 817.56) * mm, "mid": v(-15.14, 812.8) * mm, "end": v(-10.38, 817.56) * mm});
            skCircle(sketch, "E35.0.10.5", {"center": v(-15.14, 781.05) * mm, "radius": 4.76 * mm});
            skCircle(sketch, "E35.0.10.6", {"center": v(-15.14, 762) * mm, "radius": 4.76 * mm});
            skArc(sketch, "E35.0.10.7", {"start": v(-10.38, 801.69) * mm, "mid": v(-15.14, 806.45) * mm, "end": v(-19.9, 801.69) * mm});
            skArc(sketch, "E35.0.10.8", {"start": v(-19.9, 798.51) * mm, "mid": v(-15.14, 793.75) * mm, "end": v(-10.38, 798.51) * mm});
            skPoint(sketch, "E35.0.10.9", {"position": v(-15.14, 819.15) * mm});
            skPoint(sketch, "E35.0.10.10", {"position": v(-15.14, 800.1) * mm});
            skLineSegment(sketch, "E35.0.10.11", {"start": v(-19.9, 820.74) * mm, "end": v(-19.9, 817.56) * mm});
            skLineSegment(sketch, "E35.0.10.12", {"start": v(-10.38, 820.74) * mm, "end": v(-10.38, 817.56) * mm});
            skLineSegment(sketch, "E35.0.10.13", {"start": v(-10.38, 801.69) * mm, "end": v(-10.38, 798.51) * mm});
            skLineSegment(sketch, "E35.0.10.14", {"start": v(-19.9, 801.69) * mm, "end": v(-19.9, 798.51) * mm});
            skPoint(sketch, "E35.0.11.0", {"position": v(-15.14, 895.35) * mm});
            skArc(sketch, "E35.0.11.1", {"start": v(-10.38, 896.94) * mm, "mid": v(-15.14, 901.7) * mm, "end": v(-19.9, 896.94) * mm});
            skPoint(sketch, "E35.0.11.2", {"position": v(-15.14, 876.3) * mm});
            skPoint(sketch, "E35.0.11.3", {"position": v(-15.14, 857.25) * mm});
            skArc(sketch, "E35.0.11.4", {"start": v(-19.9, 893.76) * mm, "mid": v(-15.14, 889) * mm, "end": v(-10.38, 893.76) * mm});
            skCircle(sketch, "E35.0.11.5", {"center": v(-15.14, 857.25) * mm, "radius": 4.76 * mm});
            skCircle(sketch, "E35.0.11.6", {"center": v(-15.14, 838.2) * mm, "radius": 4.76 * mm});
            skArc(sketch, "E35.0.11.7", {"start": v(-10.38, 877.89) * mm, "mid": v(-15.14, 882.65) * mm, "end": v(-19.9, 877.89) * mm});
            skArc(sketch, "E35.0.11.8", {"start": v(-19.9, 874.71) * mm, "mid": v(-15.14, 869.95) * mm, "end": v(-10.38, 874.71) * mm});
            skPoint(sketch, "E35.0.11.9", {"position": v(-15.14, 895.35) * mm});
            skPoint(sketch, "E35.0.11.10", {"position": v(-15.14, 876.3) * mm});
            skLineSegment(sketch, "E35.0.11.11", {"start": v(-19.9, 896.94) * mm, "end": v(-19.9, 893.76) * mm});
            skLineSegment(sketch, "E35.0.11.12", {"start": v(-10.38, 896.94) * mm, "end": v(-10.38, 893.76) * mm});
            skLineSegment(sketch, "E35.0.11.13", {"start": v(-10.38, 877.89) * mm, "end": v(-10.38, 874.71) * mm});
            skLineSegment(sketch, "E35.0.11.14", {"start": v(-19.9, 877.89) * mm, "end": v(-19.9, 874.71) * mm});
            skPoint(sketch, "E35.0.12.0", {"position": v(-15.14, 971.55) * mm});
            skArc(sketch, "E35.0.12.1", {"start": v(-10.38, 973.14) * mm, "mid": v(-15.14, 977.9) * mm, "end": v(-19.9, 973.14) * mm});
            skPoint(sketch, "E35.0.12.2", {"position": v(-15.14, 952.5) * mm});
            skPoint(sketch, "E35.0.12.3", {"position": v(-15.14, 933.45) * mm});
            skArc(sketch, "E35.0.12.4", {"start": v(-19.9, 969.96) * mm, "mid": v(-15.14, 965.2) * mm, "end": v(-10.38, 969.96) * mm});
            skCircle(sketch, "E35.0.12.5", {"center": v(-15.14, 933.45) * mm, "radius": 4.76 * mm});
            skCircle(sketch, "E35.0.12.6", {"center": v(-15.14, 914.4) * mm, "radius": 4.76 * mm});
            skArc(sketch, "E35.0.12.7", {"start": v(-10.38, 954.09) * mm, "mid": v(-15.14, 958.85) * mm, "end": v(-19.9, 954.09) * mm});
            skArc(sketch, "E35.0.12.8", {"start": v(-19.9, 950.91) * mm, "mid": v(-15.14, 946.15) * mm, "end": v(-10.38, 950.91) * mm});
            skPoint(sketch, "E35.0.12.9", {"position": v(-15.14, 971.55) * mm});
            skPoint(sketch, "E35.0.12.10", {"position": v(-15.14, 952.5) * mm});
            skLineSegment(sketch, "E35.0.12.11", {"start": v(-19.9, 973.14) * mm, "end": v(-19.9, 969.96) * mm});
            skLineSegment(sketch, "E35.0.12.12", {"start": v(-10.38, 973.14) * mm, "end": v(-10.38, 969.96) * mm});
            skLineSegment(sketch, "E35.0.12.13", {"start": v(-10.38, 954.09) * mm, "end": v(-10.38, 950.91) * mm});
            skLineSegment(sketch, "E35.0.12.14", {"start": v(-19.9, 954.09) * mm, "end": v(-19.9, 950.91) * mm});
            skPoint(sketch, "E35.0.13.0", {"position": v(-15.14, 1047.75) * mm});
            skArc(sketch, "E35.0.13.1", {"start": v(-10.38, 1049.34) * mm, "mid": v(-15.14, 1054.1) * mm, "end": v(-19.9, 1049.34) * mm});
            skPoint(sketch, "E35.0.13.2", {"position": v(-15.14, 1028.7) * mm});
            skPoint(sketch, "E35.0.13.3", {"position": v(-15.14, 1009.65) * mm});
            skArc(sketch, "E35.0.13.4", {"start": v(-19.9, 1046.16) * mm, "mid": v(-15.14, 1041.4) * mm, "end": v(-10.38, 1046.16) * mm});
            skCircle(sketch, "E35.0.13.5", {"center": v(-15.14, 1009.65) * mm, "radius": 4.76 * mm});
            skCircle(sketch, "E35.0.13.6", {"center": v(-15.14, 990.6) * mm, "radius": 4.76 * mm});
            skArc(sketch, "E35.0.13.7", {"start": v(-10.38, 1030.29) * mm, "mid": v(-15.14, 1035.05) * mm, "end": v(-19.9, 1030.29) * mm});
            skArc(sketch, "E35.0.13.8", {"start": v(-19.9, 1027.11) * mm, "mid": v(-15.14, 1022.35) * mm, "end": v(-10.38, 1027.11) * mm});
            skPoint(sketch, "E35.0.13.9", {"position": v(-15.14, 1047.75) * mm});
            skPoint(sketch, "E35.0.13.10", {"position": v(-15.14, 1028.7) * mm});
            skLineSegment(sketch, "E35.0.13.11", {"start": v(-19.9, 1049.34) * mm, "end": v(-19.9, 1046.16) * mm});
            skLineSegment(sketch, "E35.0.13.12", {"start": v(-10.38, 1049.34) * mm, "end": v(-10.38, 1046.16) * mm});
            skLineSegment(sketch, "E35.0.13.13", {"start": v(-10.38, 1030.29) * mm, "end": v(-10.38, 1027.11) * mm});
            skLineSegment(sketch, "E35.0.13.14", {"start": v(-19.9, 1030.29) * mm, "end": v(-19.9, 1027.11) * mm});
            skPoint(sketch, "E35.0.14.0", {"position": v(-15.14, 1123.95) * mm});
            skArc(sketch, "E35.0.14.1", {"start": v(-10.38, 1125.54) * mm, "mid": v(-15.14, 1130.3) * mm, "end": v(-19.9, 1125.54) * mm});
            skPoint(sketch, "E35.0.14.2", {"position": v(-15.14, 1104.9) * mm});
            skPoint(sketch, "E35.0.14.3", {"position": v(-15.14, 1085.85) * mm});
            skArc(sketch, "E35.0.14.4", {"start": v(-19.9, 1122.36) * mm, "mid": v(-15.14, 1117.6) * mm, "end": v(-10.38, 1122.36) * mm});
            skCircle(sketch, "E35.0.14.5", {"center": v(-15.14, 1085.85) * mm, "radius": 4.76 * mm});
            skCircle(sketch, "E35.0.14.6", {"center": v(-15.14, 1066.8) * mm, "radius": 4.76 * mm});
            skArc(sketch, "E35.0.14.7", {"start": v(-10.38, 1106.49) * mm, "mid": v(-15.14, 1111.25) * mm, "end": v(-19.9, 1106.49) * mm});
            skArc(sketch, "E35.0.14.8", {"start": v(-19.9, 1103.31) * mm, "mid": v(-15.14, 1098.55) * mm, "end": v(-10.38, 1103.31) * mm});
            skPoint(sketch, "E35.0.14.9", {"position": v(-15.14, 1123.95) * mm});
            skPoint(sketch, "E35.0.14.10", {"position": v(-15.14, 1104.9) * mm});
            skLineSegment(sketch, "E35.0.14.11", {"start": v(-19.9, 1125.54) * mm, "end": v(-19.9, 1122.36) * mm});
            skLineSegment(sketch, "E35.0.14.12", {"start": v(-10.38, 1125.54) * mm, "end": v(-10.38, 1122.36) * mm});
            skLineSegment(sketch, "E35.0.14.13", {"start": v(-10.38, 1106.49) * mm, "end": v(-10.38, 1103.31) * mm});
            skLineSegment(sketch, "E35.0.14.14", {"start": v(-19.9, 1106.49) * mm, "end": v(-19.9, 1103.31) * mm});
            skPoint(sketch, "E35.0.15.0", {"position": v(-15.14, 1200.15) * mm});
            skArc(sketch, "E35.0.15.1", {"start": v(-10.38, 1201.74) * mm, "mid": v(-15.14, 1206.5) * mm, "end": v(-19.9, 1201.74) * mm});
            skPoint(sketch, "E35.0.15.2", {"position": v(-15.14, 1181.1) * mm});
            skPoint(sketch, "E35.0.15.3", {"position": v(-15.14, 1162.05) * mm});
            skArc(sketch, "E35.0.15.4", {"start": v(-19.9, 1198.56) * mm, "mid": v(-15.14, 1193.8) * mm, "end": v(-10.38, 1198.56) * mm});
            skCircle(sketch, "E35.0.15.5", {"center": v(-15.14, 1162.05) * mm, "radius": 4.76 * mm});
            skCircle(sketch, "E35.0.15.6", {"center": v(-15.14, 1143) * mm, "radius": 4.76 * mm});
            skArc(sketch, "E35.0.15.7", {"start": v(-10.38, 1182.69) * mm, "mid": v(-15.14, 1187.45) * mm, "end": v(-19.9, 1182.69) * mm});
            skArc(sketch, "E35.0.15.8", {"start": v(-19.9, 1179.51) * mm, "mid": v(-15.14, 1174.75) * mm, "end": v(-10.38, 1179.51) * mm});
            skPoint(sketch, "E35.0.15.9", {"position": v(-15.14, 1200.15) * mm});
            skPoint(sketch, "E35.0.15.10", {"position": v(-15.14, 1181.1) * mm});
            skLineSegment(sketch, "E35.0.15.11", {"start": v(-19.9, 1201.74) * mm, "end": v(-19.9, 1198.56) * mm});
            skLineSegment(sketch, "E35.0.15.12", {"start": v(-10.38, 1201.74) * mm, "end": v(-10.38, 1198.56) * mm});
            skLineSegment(sketch, "E35.0.15.13", {"start": v(-10.38, 1182.69) * mm, "end": v(-10.38, 1179.51) * mm});
            skLineSegment(sketch, "E35.0.15.14", {"start": v(-19.9, 1182.69) * mm, "end": v(-19.9, 1179.51) * mm});
            skPoint(sketch, "E35.0.16.0", {"position": v(-15.14, 1276.35) * mm});
            skArc(sketch, "E35.0.16.1", {"start": v(-10.38, 1277.94) * mm, "mid": v(-15.14, 1282.7) * mm, "end": v(-19.9, 1277.94) * mm});
            skPoint(sketch, "E35.0.16.2", {"position": v(-15.14, 1257.3) * mm});
            skPoint(sketch, "E35.0.16.3", {"position": v(-15.14, 1238.25) * mm});
            skArc(sketch, "E35.0.16.4", {"start": v(-19.9, 1274.76) * mm, "mid": v(-15.14, 1270) * mm, "end": v(-10.38, 1274.76) * mm});
            skCircle(sketch, "E35.0.16.5", {"center": v(-15.14, 1238.25) * mm, "radius": 4.76 * mm});
            skCircle(sketch, "E35.0.16.6", {"center": v(-15.14, 1219.2) * mm, "radius": 4.76 * mm});
            skArc(sketch, "E35.0.16.7", {"start": v(-10.38, 1258.89) * mm, "mid": v(-15.14, 1263.65) * mm, "end": v(-19.9, 1258.89) * mm});
            skArc(sketch, "E35.0.16.8", {"start": v(-19.9, 1255.71) * mm, "mid": v(-15.14, 1250.95) * mm, "end": v(-10.38, 1255.71) * mm});
            skPoint(sketch, "E35.0.16.9", {"position": v(-15.14, 1276.35) * mm});
            skPoint(sketch, "E35.0.16.10", {"position": v(-15.14, 1257.3) * mm});
            skLineSegment(sketch, "E35.0.16.11", {"start": v(-19.9, 1277.94) * mm, "end": v(-19.9, 1274.76) * mm});
            skLineSegment(sketch, "E35.0.16.12", {"start": v(-10.38, 1277.94) * mm, "end": v(-10.38, 1274.76) * mm});
            skLineSegment(sketch, "E35.0.16.13", {"start": v(-10.38, 1258.89) * mm, "end": v(-10.38, 1255.71) * mm});
            skLineSegment(sketch, "E35.0.16.14", {"start": v(-19.9, 1258.89) * mm, "end": v(-19.9, 1255.71) * mm});
            skPoint(sketch, "E35.0.17.0", {"position": v(-15.14, 1352.55) * mm});
            skArc(sketch, "E35.0.17.1", {"start": v(-10.38, 1354.14) * mm, "mid": v(-15.14, 1358.9) * mm, "end": v(-19.9, 1354.14) * mm});
            skPoint(sketch, "E35.0.17.2", {"position": v(-15.14, 1333.5) * mm});
            skPoint(sketch, "E35.0.17.3", {"position": v(-15.14, 1314.45) * mm});
            skArc(sketch, "E35.0.17.4", {"start": v(-19.9, 1350.96) * mm, "mid": v(-15.14, 1346.2) * mm, "end": v(-10.38, 1350.96) * mm});
            skCircle(sketch, "E35.0.17.5", {"center": v(-15.14, 1314.45) * mm, "radius": 4.76 * mm});
            skCircle(sketch, "E35.0.17.6", {"center": v(-15.14, 1295.4) * mm, "radius": 4.76 * mm});
            skArc(sketch, "E35.0.17.7", {"start": v(-10.38, 1335.09) * mm, "mid": v(-15.14, 1339.85) * mm, "end": v(-19.9, 1335.09) * mm});
            skArc(sketch, "E35.0.17.8", {"start": v(-19.9, 1331.91) * mm, "mid": v(-15.14, 1327.15) * mm, "end": v(-10.38, 1331.91) * mm});
            skPoint(sketch, "E35.0.17.9", {"position": v(-15.14, 1352.55) * mm});
            skPoint(sketch, "E35.0.17.10", {"position": v(-15.14, 1333.5) * mm});
            skLineSegment(sketch, "E35.0.17.11", {"start": v(-19.9, 1354.14) * mm, "end": v(-19.9, 1350.96) * mm});
            skLineSegment(sketch, "E35.0.17.12", {"start": v(-10.38, 1354.14) * mm, "end": v(-10.38, 1350.96) * mm});
            skLineSegment(sketch, "E35.0.17.13", {"start": v(-10.38, 1335.09) * mm, "end": v(-10.38, 1331.91) * mm});
            skLineSegment(sketch, "E35.0.17.14", {"start": v(-19.9, 1335.09) * mm, "end": v(-19.9, 1331.91) * mm});
            skPoint(sketch, "E35.0.18.0", {"position": v(-15.14, 1428.75) * mm});
            skArc(sketch, "E35.0.18.1", {"start": v(-10.38, 1430.34) * mm, "mid": v(-15.14, 1435.1) * mm, "end": v(-19.9, 1430.34) * mm});
            skPoint(sketch, "E35.0.18.2", {"position": v(-15.14, 1409.7) * mm});
            skPoint(sketch, "E35.0.18.3", {"position": v(-15.14, 1390.65) * mm});
            skArc(sketch, "E35.0.18.4", {"start": v(-19.9, 1427.16) * mm, "mid": v(-15.14, 1422.4) * mm, "end": v(-10.38, 1427.16) * mm});
            skCircle(sketch, "E35.0.18.5", {"center": v(-15.14, 1390.65) * mm, "radius": 4.76 * mm});
            skCircle(sketch, "E35.0.18.6", {"center": v(-15.14, 1371.6) * mm, "radius": 4.76 * mm});
            skArc(sketch, "E35.0.18.7", {"start": v(-10.38, 1411.29) * mm, "mid": v(-15.14, 1416.05) * mm, "end": v(-19.9, 1411.29) * mm});
            skArc(sketch, "E35.0.18.8", {"start": v(-19.9, 1408.11) * mm, "mid": v(-15.14, 1403.35) * mm, "end": v(-10.38, 1408.11) * mm});
            skPoint(sketch, "E35.0.18.9", {"position": v(-15.14, 1428.75) * mm});
            skPoint(sketch, "E35.0.18.10", {"position": v(-15.14, 1409.7) * mm});
            skLineSegment(sketch, "E35.0.18.11", {"start": v(-19.9, 1430.34) * mm, "end": v(-19.9, 1427.16) * mm});
            skLineSegment(sketch, "E35.0.18.12", {"start": v(-10.38, 1430.34) * mm, "end": v(-10.38, 1427.16) * mm});
            skLineSegment(sketch, "E35.0.18.13", {"start": v(-10.38, 1411.29) * mm, "end": v(-10.38, 1408.11) * mm});
            skLineSegment(sketch, "E35.0.18.14", {"start": v(-19.9, 1411.29) * mm, "end": v(-19.9, 1408.11) * mm});
            skPoint(sketch, "E35.0.19.0", {"position": v(-15.14, 1504.95) * mm});
            skArc(sketch, "E35.0.19.1", {"start": v(-10.38, 1506.54) * mm, "mid": v(-15.14, 1511.3) * mm, "end": v(-19.9, 1506.54) * mm});
            skPoint(sketch, "E35.0.19.2", {"position": v(-15.14, 1485.9) * mm});
            skPoint(sketch, "E35.0.19.3", {"position": v(-15.14, 1466.85) * mm});
            skArc(sketch, "E35.0.19.4", {"start": v(-19.9, 1503.36) * mm, "mid": v(-15.14, 1498.6) * mm, "end": v(-10.38, 1503.36) * mm});
            skCircle(sketch, "E35.0.19.5", {"center": v(-15.14, 1466.85) * mm, "radius": 4.76 * mm});
            skCircle(sketch, "E35.0.19.6", {"center": v(-15.14, 1447.8) * mm, "radius": 4.76 * mm});
            skArc(sketch, "E35.0.19.7", {"start": v(-10.38, 1487.49) * mm, "mid": v(-15.14, 1492.25) * mm, "end": v(-19.9, 1487.49) * mm});
            skArc(sketch, "E35.0.19.8", {"start": v(-19.9, 1484.31) * mm, "mid": v(-15.14, 1479.55) * mm, "end": v(-10.38, 1484.31) * mm});
            skPoint(sketch, "E35.0.19.9", {"position": v(-15.14, 1504.95) * mm});
            skPoint(sketch, "E35.0.19.10", {"position": v(-15.14, 1485.9) * mm});
            skLineSegment(sketch, "E35.0.19.11", {"start": v(-19.9, 1506.54) * mm, "end": v(-19.9, 1503.36) * mm});
            skLineSegment(sketch, "E35.0.19.12", {"start": v(-10.38, 1506.54) * mm, "end": v(-10.38, 1503.36) * mm});
            skLineSegment(sketch, "E35.0.19.13", {"start": v(-10.38, 1487.49) * mm, "end": v(-10.38, 1484.31) * mm});
            skLineSegment(sketch, "E35.0.19.14", {"start": v(-19.9, 1487.49) * mm, "end": v(-19.9, 1484.31) * mm});
            skPoint(sketch, "E35.0.20.0", {"position": v(-15.14, 1581.15) * mm});
            skArc(sketch, "E35.0.20.1", {"start": v(-10.38, 1582.74) * mm, "mid": v(-15.14, 1587.5) * mm, "end": v(-19.9, 1582.74) * mm});
            skPoint(sketch, "E35.0.20.2", {"position": v(-15.14, 1562.1) * mm});
            skPoint(sketch, "E35.0.20.3", {"position": v(-15.14, 1543.05) * mm});
            skArc(sketch, "E35.0.20.4", {"start": v(-19.9, 1579.56) * mm, "mid": v(-15.14, 1574.8) * mm, "end": v(-10.38, 1579.56) * mm});
            skCircle(sketch, "E35.0.20.5", {"center": v(-15.14, 1543.05) * mm, "radius": 4.76 * mm});
            skCircle(sketch, "E35.0.20.6", {"center": v(-15.14, 1524) * mm, "radius": 4.76 * mm});
            skArc(sketch, "E35.0.20.7", {"start": v(-10.38, 1563.69) * mm, "mid": v(-15.14, 1568.45) * mm, "end": v(-19.9, 1563.69) * mm});
            skArc(sketch, "E35.0.20.8", {"start": v(-19.9, 1560.51) * mm, "mid": v(-15.14, 1555.75) * mm, "end": v(-10.38, 1560.51) * mm});
            skPoint(sketch, "E35.0.20.9", {"position": v(-15.14, 1581.15) * mm});
            skPoint(sketch, "E35.0.20.10", {"position": v(-15.14, 1562.1) * mm});
            skLineSegment(sketch, "E35.0.20.11", {"start": v(-19.9, 1582.74) * mm, "end": v(-19.9, 1579.56) * mm});
            skLineSegment(sketch, "E35.0.20.12", {"start": v(-10.38, 1582.74) * mm, "end": v(-10.38, 1579.56) * mm});
            skLineSegment(sketch, "E35.0.20.13", {"start": v(-10.38, 1563.69) * mm, "end": v(-10.38, 1560.51) * mm});
            skLineSegment(sketch, "E35.0.20.14", {"start": v(-19.9, 1563.69) * mm, "end": v(-19.9, 1560.51) * mm});
            skPoint(sketch, "E35.0.21.0", {"position": v(-15.14, 1657.35) * mm});
            skArc(sketch, "E35.0.21.1", {"start": v(-10.38, 1658.94) * mm, "mid": v(-15.14, 1663.7) * mm, "end": v(-19.9, 1658.94) * mm});
            skPoint(sketch, "E35.0.21.2", {"position": v(-15.14, 1638.3) * mm});
            skPoint(sketch, "E35.0.21.3", {"position": v(-15.14, 1619.25) * mm});
            skArc(sketch, "E35.0.21.4", {"start": v(-19.9, 1655.76) * mm, "mid": v(-15.14, 1651) * mm, "end": v(-10.38, 1655.76) * mm});
            skCircle(sketch, "E35.0.21.5", {"center": v(-15.14, 1619.25) * mm, "radius": 4.76 * mm});
            skCircle(sketch, "E35.0.21.6", {"center": v(-15.14, 1600.2) * mm, "radius": 4.76 * mm});
            skArc(sketch, "E35.0.21.7", {"start": v(-10.38, 1639.89) * mm, "mid": v(-15.14, 1644.65) * mm, "end": v(-19.9, 1639.89) * mm});
            skArc(sketch, "E35.0.21.8", {"start": v(-19.9, 1636.71) * mm, "mid": v(-15.14, 1631.95) * mm, "end": v(-10.38, 1636.71) * mm});
            skPoint(sketch, "E35.0.21.9", {"position": v(-15.14, 1657.35) * mm});
            skPoint(sketch, "E35.0.21.10", {"position": v(-15.14, 1638.3) * mm});
            skLineSegment(sketch, "E35.0.21.11", {"start": v(-19.9, 1658.94) * mm, "end": v(-19.9, 1655.76) * mm});
            skLineSegment(sketch, "E35.0.21.12", {"start": v(-10.38, 1658.94) * mm, "end": v(-10.38, 1655.76) * mm});
            skLineSegment(sketch, "E35.0.21.13", {"start": v(-10.38, 1639.89) * mm, "end": v(-10.38, 1636.71) * mm});
            skLineSegment(sketch, "E35.0.21.14", {"start": v(-19.9, 1639.89) * mm, "end": v(-19.9, 1636.71) * mm});
            skPoint(sketch, "E35.0.22.0", {"position": v(-15.14, 1733.55) * mm});
            skArc(sketch, "E35.0.22.1", {"start": v(-10.38, 1735.14) * mm, "mid": v(-15.14, 1739.9) * mm, "end": v(-19.9, 1735.14) * mm});
            skPoint(sketch, "E35.0.22.2", {"position": v(-15.14, 1714.5) * mm});
            skPoint(sketch, "E35.0.22.3", {"position": v(-15.14, 1695.45) * mm});
            skArc(sketch, "E35.0.22.4", {"start": v(-19.9, 1731.96) * mm, "mid": v(-15.14, 1727.2) * mm, "end": v(-10.38, 1731.96) * mm});
            skCircle(sketch, "E35.0.22.5", {"center": v(-15.14, 1695.45) * mm, "radius": 4.76 * mm});
            skCircle(sketch, "E35.0.22.6", {"center": v(-15.14, 1676.4) * mm, "radius": 4.76 * mm});
            skArc(sketch, "E35.0.22.7", {"start": v(-10.38, 1716.09) * mm, "mid": v(-15.14, 1720.85) * mm, "end": v(-19.9, 1716.09) * mm});
            skArc(sketch, "E35.0.22.8", {"start": v(-19.9, 1712.91) * mm, "mid": v(-15.14, 1708.15) * mm, "end": v(-10.38, 1712.91) * mm});
            skPoint(sketch, "E35.0.22.9", {"position": v(-15.14, 1733.55) * mm});
            skPoint(sketch, "E35.0.22.10", {"position": v(-15.14, 1714.5) * mm});
            skLineSegment(sketch, "E35.0.22.11", {"start": v(-19.9, 1735.14) * mm, "end": v(-19.9, 1731.96) * mm});
            skLineSegment(sketch, "E35.0.22.12", {"start": v(-10.38, 1735.14) * mm, "end": v(-10.38, 1731.96) * mm});
            skLineSegment(sketch, "E35.0.22.13", {"start": v(-10.38, 1716.09) * mm, "end": v(-10.38, 1712.91) * mm});
            skLineSegment(sketch, "E35.0.22.14", {"start": v(-19.9, 1716.09) * mm, "end": v(-19.9, 1712.91) * mm});
            skPoint(sketch, "E35.0.23.0", {"position": v(-15.14, 1809.75) * mm});
            skArc(sketch, "E35.0.23.1", {"start": v(-10.38, 1811.34) * mm, "mid": v(-15.14, 1816.1) * mm, "end": v(-19.9, 1811.34) * mm});
            skPoint(sketch, "E35.0.23.2", {"position": v(-15.14, 1790.7) * mm});
            skPoint(sketch, "E35.0.23.3", {"position": v(-15.14, 1771.65) * mm});
            skArc(sketch, "E35.0.23.4", {"start": v(-19.9, 1808.16) * mm, "mid": v(-15.14, 1803.4) * mm, "end": v(-10.38, 1808.16) * mm});
            skCircle(sketch, "E35.0.23.5", {"center": v(-15.14, 1771.65) * mm, "radius": 4.76 * mm});
            skCircle(sketch, "E35.0.23.6", {"center": v(-15.14, 1752.6) * mm, "radius": 4.76 * mm});
            skArc(sketch, "E35.0.23.7", {"start": v(-10.38, 1792.29) * mm, "mid": v(-15.14, 1797.05) * mm, "end": v(-19.9, 1792.29) * mm});
            skArc(sketch, "E35.0.23.8", {"start": v(-19.9, 1789.11) * mm, "mid": v(-15.14, 1784.35) * mm, "end": v(-10.38, 1789.11) * mm});
            skPoint(sketch, "E35.0.23.9", {"position": v(-15.14, 1809.75) * mm});
            skPoint(sketch, "E35.0.23.10", {"position": v(-15.14, 1790.7) * mm});
            skLineSegment(sketch, "E35.0.23.11", {"start": v(-19.9, 1811.34) * mm, "end": v(-19.9, 1808.16) * mm});
            skLineSegment(sketch, "E35.0.23.12", {"start": v(-10.38, 1811.34) * mm, "end": v(-10.38, 1808.16) * mm});
            skLineSegment(sketch, "E35.0.23.13", {"start": v(-10.38, 1792.29) * mm, "end": v(-10.38, 1789.11) * mm});
            skLineSegment(sketch, "E35.0.23.14", {"start": v(-19.9, 1792.29) * mm, "end": v(-19.9, 1789.11) * mm});
            skLineSegment(sketch, "E35.direction1", {"start": v(-15.14, 0) * mm, "end": v(10.99, 0) * mm, "construction": true});
            skLineSegment(sketch, "E35.direction2", {"start": v(-15.14, 0) * mm, "end": v(-15.14, 76.2) * mm, "construction": true});
            skSolve(sketch);
        }
        {
            var Q0;
            Q0=qSketchRegion(id+"F3",true);
            extrude(context, id + "F5", {"entities" : qUnion([Q0]), "operationType" : NewBodyOperationType.REMOVE, "endBound" : BoundingType.THROUGH_ALL, "oppositeDirection" : true, "depth" : 25.4 * mm, "offsetDistance" : 25.4 * mm});
        }
        {
            var Q0;
            Q0=qSketchRegion(id+"F4",true);
            extrude(context, id + "F6", {"entities" : qUnion([Q0]), "operationType" : NewBodyOperationType.REMOVE, "endBound" : BoundingType.THROUGH_ALL, "oppositeDirection" : true, "depth" : 25.4 * mm, "offsetDistance" : 25.4 * mm});
        }
        {
            var Q0;
            Q0=makeQuery(id+"F2.opExtrude","SWEPT_FACE",FACE,{"disambiguationData":[OSD([sQuery(id+"F1.wireOp",EDGE,"E1")])]});
            var sketch = newSketch(context, id + "F7", { "sketchPlane" : qUnion([Q0])});
            skLineSegment(sketch, "E36", {"start": v(1.37, 381) * mm, "end": v(-28.75, 381) * mm});
            skLineSegment(sketch, "E37", {"start": v(-28.75, 381) * mm, "end": v(-28.75, 350.88) * mm});
            skLineSegment(sketch, "E38", {"start": v(-28.75, 350.88) * mm, "end": v(1.37, 381) * mm});
            skLineSegment(sketch, "E39", {"start": v(-28.75, 0) * mm, "end": v(1.37, 0) * mm});
            skLineSegment(sketch, "E40", {"start": v(1.37, 0) * mm, "end": v(-28.75, 30.12) * mm});
            skLineSegment(sketch, "E41", {"start": v(-28.75, 30.12) * mm, "end": v(-28.75, 0) * mm});
            skSolve(sketch);
        }
        {
            var Q0;
            Q0=qSketchRegion(id+"F7",true);
            extrude(context, id + "F8", {"entities" : qUnion([Q0]), "operationType" : NewBodyOperationType.REMOVE, "endBound" : BoundingType.THROUGH_ALL, "oppositeDirection" : true, "depth" : 25.4 * mm, "offsetDistance" : 25.4 * mm});
        }
        {
            var Q0;
            Q0=makeQuery(id+"F2.opExtrude","SWEPT_BODY",BODY,{"disambiguationData":[OSD([sQuery(id+"F1.wireOp",EDGE,"E0"),sQuery(id+"F1.wireOp",EDGE,"E1"),sQuery(id+"F1.wireOp",EDGE,"E2"),sQuery(id+"F1.wireOp",EDGE,"E3"),sQuery(id+"F1.wireOp",EDGE,"E4"),sQuery(id+"F1.wireOp",EDGE,"E5")])]});
            var Q1;
            Q1=qCreatedBy(makeId("Top.planeOp"),FACE);
            mirror(context, id + "F9", {"entities" : qUnion([Q0]), "mirrorPlane" : qUnion([Q1])});
        }
        {
            var Q0;
            Q0=makeQuery(id+"F2.opExtrude","SWEPT_BODY",BODY,{"disambiguationData":[OSD([sQuery(id+"F1.wireOp",EDGE,"E0"),sQuery(id+"F1.wireOp",EDGE,"E1"),sQuery(id+"F1.wireOp",EDGE,"E2"),sQuery(id+"F1.wireOp",EDGE,"E3"),sQuery(id+"F1.wireOp",EDGE,"E4"),sQuery(id+"F1.wireOp",EDGE,"E5")])]});
            deleteBodies(context, id + "F10", {"entities" : qUnion([Q0])});
        }
        {
            var Q0;
            Q0=makeQuery(id+"F9.opPattern","COPY",FACE,{"derivedFrom":makeQuery(id+"F2.opExtrude","SWEPT_FACE",FACE,{"disambiguationData":[OSD([sQuery(id+"F1.wireOp",EDGE,"E0")])]}),"instanceName":"1"});
            var sketch = newSketch(context, id + "F11", { "sketchPlane" : qUnion([Q0])});
            skLineSegment(sketch, "E42", {"start": v(15.14, -273.05) * mm, "end": v(15.14, -279.4) * mm, "construction": true});
            skPoint(sketch, "E43", {"position": v(15.14, -276.22) * mm});
            skCircle(sketch, "E44", {"center": v(17.68, -276.22) * mm, "radius": 9.52 * mm});
            skLineSegment(sketch, "E45", {"start": v(15.14, -80.96) * mm, "end": v(15.14, -90.49) * mm, "construction": true});
            skPoint(sketch, "E45.startSnap0", {"position": v(15.14, -63.5) * mm});
            skPoint(sketch, "E46", {"position": v(15.14, -85.72) * mm});
            skCircle(sketch, "E47", {"center": v(17.68, -85.72) * mm, "radius": 9.53 * mm});
            skPoint(sketch, "E48", {"position": v(15.14, -107.95) * mm});
            skSolve(sketch);
        }
        {
            var Q0;
            {var subQ0=makeQuery(id+"F2.opExtrude","SWEPT_FACE",FACE,{"disambiguationData":[OSD([sQuery(id+"F1.wireOp",EDGE,"E0")])]});var subQ2=makeQuery(id+"F9.opPattern","COPY",EDGE,{"derivedFrom":makeQuery(id+"F6.boolean.opBoolean","INTERSECT",EDGE,{"derivedFrom":[subQ0,makeQuery(id+"F6.opExtrude","SWEPT_FACE",FACE,{"disambiguationData":[OSD([sQuery(id+"F4.wireOp",EDGE,"E35.0.3.7")])]})]}),"instanceName":"1"});var subQ4=sQuery(id+"F11.wireOp",EDGE,"E44");var subQ5=makeQuery(id+"F11.imprint","INTERSECT",VERTEX,{"derivedFrom":[subQ2,subQ4]});Q0=makeQuery(id+"F11.imprint","IMPRINT",FACE,{"disambiguationData":[TD([[makeQuery(id+"F11.imprint","IMPRINT",EDGE,{"disambiguationData":[TD([[subQ5,-1.0]])],"derivedFrom":subQ4}),1.0]])]});}
            var Q1;
            {var subQ0=sQuery(id+"F11.wireOp",EDGE,"E47");var subQ1=makeQuery(id+"F2.opExtrude","SWEPT_FACE",FACE,{"disambiguationData":[OSD([sQuery(id+"F1.wireOp",EDGE,"E0")])]});var subQ2=makeQuery(id+"F9.opPattern","COPY",EDGE,{"derivedFrom":makeQuery(id+"F6.boolean.opBoolean","INTERSECT",EDGE,{"derivedFrom":[subQ1,makeQuery(id+"F6.opExtrude","SWEPT_FACE",FACE,{"disambiguationData":[OSD([sQuery(id+"F4.wireOp",EDGE,"E35.0.1.6")])]})]}),"instanceName":"1"});var subQ3=makeQuery(id+"F11.imprint","INTERSECT",VERTEX,{"disambiguationData":[OD(0.0)],"derivedFrom":[subQ2,subQ0]});Q1=makeQuery(id+"F11.imprint","IMPRINT",FACE,{"disambiguationData":[TD([[makeQuery(id+"F11.imprint","IMPRINT",EDGE,{"disambiguationData":[TD([[subQ3,-1.0]])],"derivedFrom":subQ0}),1.0]])]});}
            extrude(context, id + "F12", {"entities" : qUnion([Q0, Q1]), "operationType" : NewBodyOperationType.REMOVE, "endBound" : BoundingType.THROUGH_ALL, "oppositeDirection" : true, "depth" : 25.4 * mm, "offsetDistance" : 25.4 * mm});
        }
        {
            var Q0;
            Q0=makeQuery(id+"F9.opPattern","COPY",FACE,{"derivedFrom":makeQuery(id+"F2.opExtrude","SWEPT_FACE",FACE,{"disambiguationData":[OSD([sQuery(id+"F1.wireOp",EDGE,"E0")])]}),"instanceName":"1"});
            var sketch = newSketch(context, id + "F13", { "sketchPlane" : qUnion([Q0])});
            skLineSegment(sketch, "E49", {"start": v(19.9, -361.95) * mm, "end": v(10.38, -361.95) * mm, "construction": true});
            skPoint(sketch, "E50", {"position": v(15.14, -361.95) * mm});
            skSolve(sketch);
        }
        {
            var Q0;
            Q0=makeQuery(id+"F9.opPattern","COPY",FACE,{"derivedFrom":makeQuery(id+"F2.opExtrude","SWEPT_FACE",FACE,{"disambiguationData":[OSD([sQuery(id+"F1.wireOp",EDGE,"E4")])]}),"instanceName":"1"});
            var sketch = newSketch(context, id + "F14", { "sketchPlane" : qUnion([Q0])});
            skLineSegment(sketch, "E51", {"start": v(-19.9, -361.95) * mm, "end": v(-10.38, -361.95) * mm, "construction": true});
            skPoint(sketch, "E52", {"position": v(-15.14, -361.95) * mm});
            skSolve(sketch);
        }
    });
